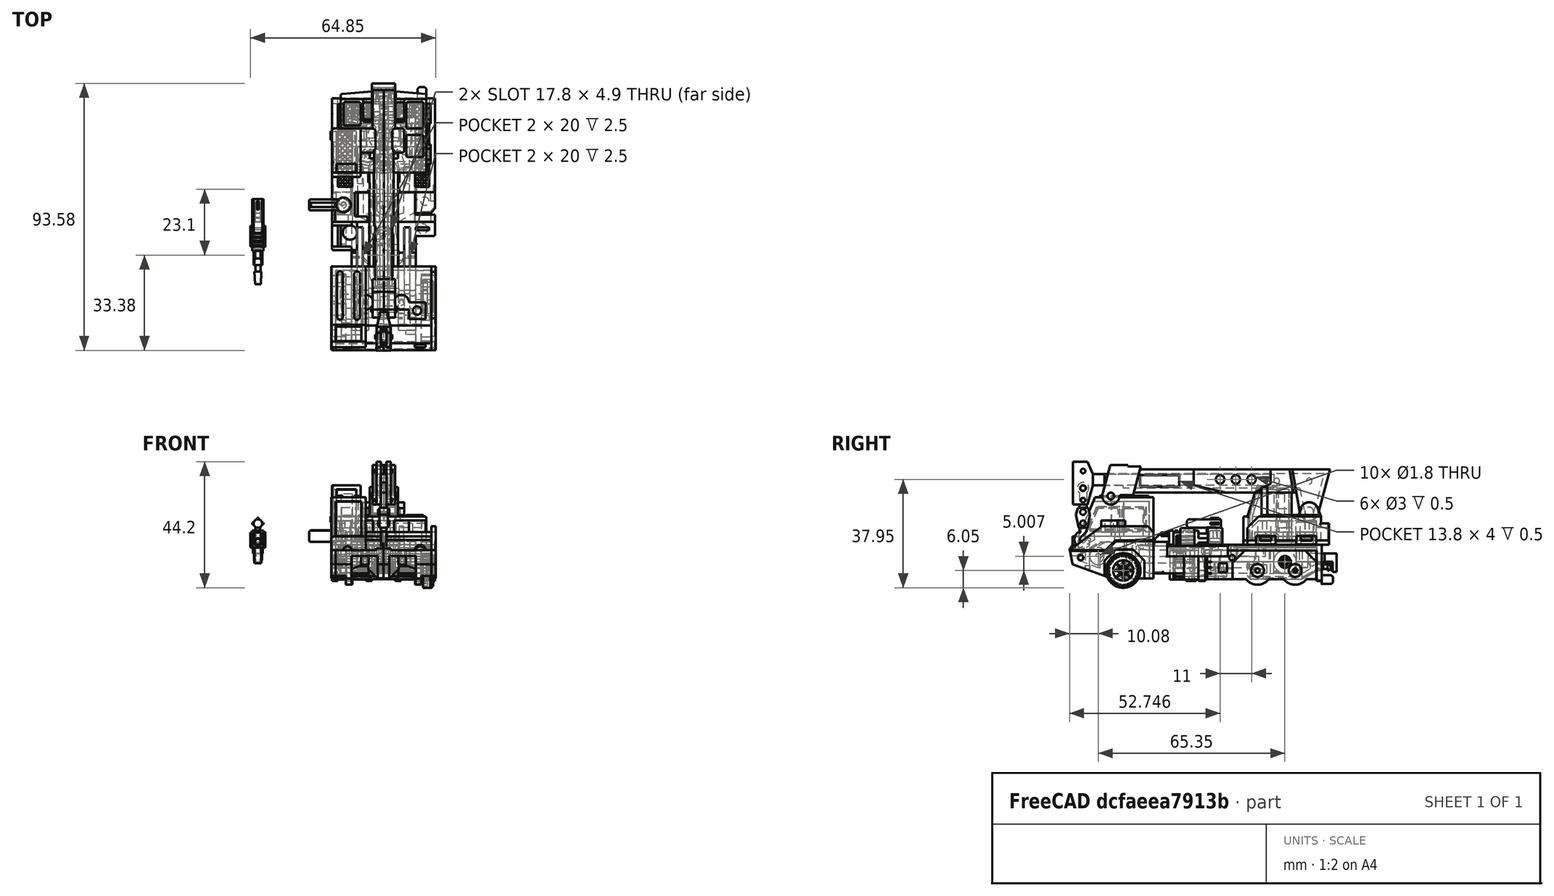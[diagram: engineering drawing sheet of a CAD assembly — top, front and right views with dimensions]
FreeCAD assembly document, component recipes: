
FREECAD ASSEMBLY — COMPONENT RECIPES ("Hook")

This assembly document has 27 components, labeled P0..P26 below (a component is one placed body or linked part). 27 of them carry a construction recipe — the FreeCAD feature program that regenerates the part from scratch, quoted from this document or its linked companion documents; the rest are supplied as boundary geometry only. No exploded tour is included for this assembly.
NOTE — document 4 of 5 of this assembly tour. The two overview renders and the header above are repeated from document 1; the component sections below continue where the previous document stopped.
COMPONENT P17 — recipe-attached ("Left_Outer_Leg", modeled in this document).
Construction recipe (the document's own serialized feature program — sketch geometry with constraints, then the solid features built on it; lengths are millimeters unless a unit is written):

FEATURE [PartDesign::SubShapeBinder] Binder013
  BindCopyOnChange = 0
  BindMode = 0
  ClaimChildren = false
  Context = -> Body019 [Binder013.]
  Fuse = false
  MakeFace = true
  OffsetFill = false
  OffsetIntersection = false
  OffsetJoinType = 0
  OffsetOpenResult = false
  PartialLoad = false
  Refine = true
  Relative = true
  Support = -> [Part__Mirroring001[Face7]]
  _Version = 2
FEATURE [Sketcher::SketchObject] Sketch288
  ArcFitTolerance = 1e-06
  AttachmentSupport = -> [Binder013]
  ExternalGeometry = -> [Binder013]
  FullyConstrained = true
  MakeInternals = false
  MapMode = 5
  Placement = pos=(1.25,0,0) rot=(0.57735,-0.57735,-0.57735;2.0944rad)
  sketch-geometry (39):
    g0: LineSegment StartX=17.1313 StartY=-9.8 StartZ=0 EndX=17.1313 EndY=18.7 EndZ=0
    g1: LineSegment StartX=17.1313 StartY=-9.8 StartZ=0 EndX=18.8313 EndY=-9.8 EndZ=0
    g2: LineSegment StartX=18.8313 StartY=-9.8 StartZ=0 EndX=18.8313 EndY=-3.6 EndZ=0
    g3: Circle CenterX=41.1657 CenterY=-2.53692 CenterZ=0 NormalX=0 NormalY=0 NormalZ=1 AngleXU=0 Radius=0.95
    g4: LineSegment StartX=18.8313 StartY=-3.6 StartZ=0 EndX=22.7813 EndY=0.35 EndZ=0
    g5: LineSegment StartX=22.7813 StartY=0.35 StartZ=0 EndX=28.8813 EndY=0.35 EndZ=0
    g6: LineSegment StartX=28.8813 StartY=0.35 StartZ=0 EndX=32.8313 EndY=-3.6 EndZ=0
    g7: LineSegment StartX=32.8313 StartY=-3.6 StartZ=0 EndX=32.8313 EndY=-8.93216 EndZ=0
    g8: LineSegment StartX=32.8313 StartY=-8.93216 StartZ=0 EndX=44.062 EndY=-4.89651 EndZ=0
    g9: LineSegment StartX=44.062 StartY=-4.89651 StartZ=0 EndX=44.9561 EndY=0.0557565 EndZ=0
    g10: LineSegment StartX=44.9561 StartY=0.0557565 StartZ=0 EndX=43.9561 EndY=0.0557565 EndZ=0
    g11: LineSegment StartX=43.9561 StartY=0.0557565 StartZ=0 EndX=43.9561 EndY=5 EndZ=0
    g12: LineSegment StartX=43.9561 StartY=5 StartZ=0 EndX=41.9561 EndY=5 EndZ=0
    g13: LineSegment StartX=17.1313 StartY=18.7 StartZ=0 EndX=36.1313 EndY=18.7 EndZ=0
    g14: LineSegment StartX=36.1313 StartY=18.7 StartZ=0 EndX=41.9561 EndY=5 EndZ=0
    g15: LineSegment StartX=18.9313 StartY=14.2 StartZ=0 EndX=18.9313 EndY=8.1 EndZ=0
    g16: LineSegment StartX=19.4313 StartY=7.6 StartZ=0 EndX=25.5313 EndY=7.6 EndZ=0
    g17: LineSegment StartX=26.0313 StartY=8.1 StartZ=0 EndX=26.0313 EndY=14.2 EndZ=0
    g18: LineSegment StartX=25.5313 StartY=14.7 StartZ=0 EndX=19.4313 EndY=14.7 EndZ=0
    g19: LineSegment StartX=28.5313 StartY=14.7 StartZ=0 EndX=34.8006 EndY=14.7 EndZ=0
    g20: LineSegment StartX=35.2607 StartY=14.3956 StartZ=0 EndX=37.8542 EndY=8.29564 EndZ=0
    g21: LineSegment StartX=37.3941 StartY=7.6 StartZ=0 EndX=28.5313 EndY=7.6 EndZ=0
    g22: LineSegment StartX=28.0313 StartY=8.1 StartZ=0 EndX=28.0313 EndY=14.2 EndZ=0
    g23: ArcOfCircle CenterX=37.3941 CenterY=8.1 CenterZ=0 NormalX=0 NormalY=0 NormalZ=1 AngleXU=0 Radius=0.5 StartAngle=4.71239 EndAngle=6.6852
    g24: GeomPoint [constr] X=38.15 Y=7.6 Z=0
    g25: ArcOfCircle CenterX=34.8006 CenterY=14.2 CenterZ=0 NormalX=0 NormalY=0 NormalZ=1 AngleXU=0 Radius=0.5 StartAngle=0.402012 EndAngle=1.5708
    g26: GeomPoint [constr] X=35.1313 Y=14.7 Z=0
    g27: ArcOfCircle CenterX=28.5313 CenterY=14.2 CenterZ=0 NormalX=0 NormalY=0 NormalZ=1 AngleXU=0 Radius=0.5 StartAngle=1.5708 EndAngle=3.14159
    g28: GeomPoint [constr] X=28.0313 Y=14.7 Z=0
    g29: ArcOfCircle CenterX=28.5313 CenterY=8.1 CenterZ=0 NormalX=0 NormalY=0 NormalZ=1 AngleXU=0 Radius=0.5 StartAngle=3.14159 EndAngle=4.71239
    g30: GeomPoint [constr] X=28.0313 Y=7.6 Z=0
    g31: ArcOfCircle CenterX=25.5313 CenterY=8.1 CenterZ=0 NormalX=0 NormalY=0 NormalZ=1 AngleXU=0 Radius=0.5 StartAngle=4.71239 EndAngle=6.28319
    g32: GeomPoint [constr] X=26.0313 Y=7.6 Z=0
    g33: ArcOfCircle CenterX=25.5313 CenterY=14.2 CenterZ=0 NormalX=0 NormalY=0 NormalZ=1 AngleXU=0 Radius=0.5 StartAngle=1.2e-15 EndAngle=1.5708
    g34: GeomPoint [constr] X=26.0313 Y=14.7 Z=0
    g35: ArcOfCircle CenterX=19.4313 CenterY=14.2 CenterZ=0 NormalX=0 NormalY=0 NormalZ=1 AngleXU=0 Radius=0.5 StartAngle=1.5708 EndAngle=3.14159
    g36: GeomPoint [constr] X=18.9313 Y=14.7 Z=0
    g37: ArcOfCircle CenterX=19.4313 CenterY=8.1 CenterZ=0 NormalX=0 NormalY=0 NormalZ=1 AngleXU=0 Radius=0.5 StartAngle=3.14159 EndAngle=4.71239
    g38: GeomPoint [constr] X=18.9313 Y=7.6 Z=0
  constraints (91):
    c: Coincident(g0,g-4)
    c: Vertical(g0)
    c: DistanceY(g0,g0) = 28.5
    c: Coincident(g1,g0)
    c: Coincident(g1,g-5)
    c: Coincident(g2,g1)
    c: Coincident(g3,g-13)
    c: Coincident(g2,g-6)
    c: Coincident(g4,g2)
    c: Coincident(g4,g-7)
    c: Coincident(g5,g4)
    c: Coincident(g5,g-8)
    c: Coincident(g6,g5)
    c: Coincident(g6,g-9)
    c: Coincident(g7,g6)
    c: Coincident(g7,g-10)
    c: Coincident(g8,g7)
    c: Coincident(g8,g-11)
    c: Coincident(g9,g8)
    c: Coincident(g9,g-12)
    c: Coincident(g10,g9)
    c: DistanceX(g10,g10) = 1
    c: Coincident(g11,g10)
    c: Vertical(g11)
    c: Coincident(g12,g11)
    c: Horizontal(g12)
    c: Coincident(g13,g0)
    c: Horizontal(g13)
    c: Coincident(g14,g13)
    c: Coincident(g14,g12)
    c: Radius(g3) = 0.95
    c: DistanceY(g-14,g12) = 0
    c: DistanceX(g12,g12) = 2
    c: DistanceX(g13,g13) = 19
    c: PointOnObject(g10,g-12)
    c: Vertical(g15)
    c: Vertical(g17)
    c: Horizontal(g16)
    c: Horizontal(g18)
    c: Horizontal(g19)
    c: Horizontal(g21)
    c: Vertical(g22)
    c: DistanceX(g36,g34) = 7.1
    c: DistanceY(g38,g36) = 7.1
    c: DistanceX(g28,g26) = 7.1
    c: Parallel(g20,g14)
    c: DistanceX(g0,g36) = 1.8
    c: DistanceY(g36,g0) = 4
    c: DistanceY(g30,g28) = 7.1
    c: DistanceY(g26,g13) = 4
    c: DistanceX(g34,g28) = 2
    c: PointOnObject(g24,g20)
    c: PointOnObject(g24,g21)
    c: Tangent(g20,g23) = 1.5708
    c: Tangent(g21,g23) = 1.5708
    c: PointOnObject(g26,g19)
    c: PointOnObject(g26,g20)
    c: Tangent(g19,g25) = 1.5708
    c: Tangent(g20,g25) = 1.5708
    c: PointOnObject(g28,g19)
    c: PointOnObject(g28,g22)
    c: Tangent(g19,g27) = 1.5708
    c: Tangent(g22,g27) = 1.5708
    c: PointOnObject(g30,g21)
    c: PointOnObject(g30,g22)
    c: Tangent(g21,g29) = 1.5708
    c: Tangent(g22,g29) = 1.5708
    c: PointOnObject(g32,g16)
    c: PointOnObject(g32,g17)
    c: Tangent(g16,g31) = -1.5708
    c: Tangent(g17,g31) = -1.5708
    c: PointOnObject(g34,g17)
    c: PointOnObject(g34,g18)
    c: Tangent(g17,g33) = -1.5708
    c: Tangent(g18,g33) = -1.5708
    c: PointOnObject(g36,g15)
    c: PointOnObject(g36,g18)
    c: Tangent(g15,g35) = -1.5708
    c: Tangent(g18,g35) = -1.5708
    c: PointOnObject(g38,g15)
    c: PointOnObject(g38,g16)
    c: Tangent(g15,g37) = -1.5708
    c: Tangent(g16,g37) = -1.5708
    c: Radius(g37) = 0.5
    c: Radius(g35) = 0.5
    c: Radius(g33) = 0.5
    c: Radius(g31) = 0.5
    c: Radius(g29) = 0.5
    c: Radius(g27) = 0.5
    c: Radius(g23) = 0.5
    c: Radius(g25) = 0.5
FEATURE [PartDesign::Pad] Pad188
  Direction = (-1,0,0)
  Length = 1.5
  Length2 = 10
  Profile = -> Sketch288
  ReferenceAxis = -> Sketch288 [N_Axis]
  Refine = true
  Suppressed = false
  Type = 0
FEATURE [Sketcher::SketchObject] Sketch289
  ArcFitTolerance = 1e-06
  AttachmentSupport = -> [Pad188]
  ExternalGeometry = -> [Pad188]
  FullyConstrained = true
  MakeInternals = false
  MapMode = 5
  Placement = pos=(0,-17.1313,0) rot=(0,0.707107,0.707107;3.14159rad)
  sketch-geometry (8):
    g0: LineSegment StartX=0.25 StartY=18.7 StartZ=0 EndX=-11.75 EndY=18.7 EndZ=0
    g1: LineSegment StartX=-11.75 StartY=18.7 StartZ=0 EndX=-11.75 EndY=5 EndZ=0
    g2: LineSegment StartX=-11.75 StartY=5 StartZ=0 EndX=-18 EndY=5 EndZ=0
    g3: LineSegment StartX=-18 StartY=5 StartZ=0 EndX=-18 EndY=3 EndZ=0
    g4: LineSegment StartX=-18 StartY=3 StartZ=0 EndX=-6.75 EndY=3 EndZ=0
    g5: LineSegment StartX=-6.75 StartY=3 StartZ=0 EndX=-6.75 EndY=-9.8 EndZ=0
    g6: LineSegment StartX=-6.75 StartY=-9.8 StartZ=0 EndX=0.25 EndY=-9.8 EndZ=0
    g7: LineSegment StartX=0.25 StartY=-9.8 StartZ=0 EndX=0.25 EndY=18.7 EndZ=0
  constraints (22):
    c: Coincident(g0,g-4)
    c: Horizontal(g0)
    c: Coincident(g1,g0)
    c: Vertical(g1)
    c: Coincident(g2,g1)
    c: Horizontal(g2)
    c: Coincident(g3,g2)
    c: Vertical(g3)
    c: Coincident(g4,g3)
    c: Horizontal(g4)
    c: Coincident(g5,g4)
    c: Vertical(g5)
    c: Coincident(g6,g5)
    c: Coincident(g6,g-4)
    c: Horizontal(g6)
    c: DistanceX(g0,g0) = 12
    c: DistanceY(g1,g1) = 13.7
    c: DistanceX(g2,g2) = 6.25
    c: DistanceY(g3,g3) = 2
    c: DistanceX(g4,g4) = 11.25
    c: Coincident(g7,g6)
    c: Coincident(g7,g0)
FEATURE [PartDesign::Pad] Pad189
  BaseFeature = -> Pad188
  Direction = (0,1,-2e-16)
  Length = 1.5
  Length2 = 10
  Profile = -> Sketch289
  ReferenceAxis = -> Sketch289 [N_Axis]
  Refine = true
  Suppressed = false
  Type = 0
FEATURE [Sketcher::SketchObject] Sketch290
  ArcFitTolerance = 1e-06
  AttachmentSupport = -> [Pad189]
  ExternalGeometry = -> [Pad189]
  FullyConstrained = true
  MakeInternals = false
  MapMode = 5
  Placement = pos=(1.25,0,0) rot=(0.57735,0.57735,0.57735;2.0944rad)
  sketch-geometry (5):
    g0: LineSegment StartX=-41.9561 StartY=5 StartZ=0 EndX=-43.9561 EndY=5 EndZ=0
    g1: LineSegment StartX=-43.9561 StartY=5 StartZ=0 EndX=-43.9561 EndY=0.0557565 EndZ=0
    g2: LineSegment StartX=-42.7061 StartY=0.0557565 StartZ=0 EndX=-43.9561 EndY=0.0557565 EndZ=0
    g3: LineSegment StartX=-41.9561 StartY=5 StartZ=0 EndX=-41.9561 EndY=0.488769 EndZ=0
    g4: LineSegment StartX=-42.7061 StartY=0.0557565 StartZ=0 EndX=-41.9561 EndY=0.488769 EndZ=0
  constraints (12):
    c: Coincident(g0,g-3)
    c: Coincident(g0,g-4)
    c: Coincident(g1,g0)
    c: Coincident(g1,g-4)
    c: Horizontal(g2)
    c: Coincident(g2,g1)
    c: Coincident(g3,g0)
    c: Vertical(g3)
    c: Coincident(g4,g2)
    c: Coincident(g4,g3)
    c: DistanceX(g2,g2) = 1.25
    c: Angle(g4,g2) = 2.61799
FEATURE [PartDesign::Pad] Pad190
  BaseFeature = -> Pad189
  Direction = (1,0,0)
  Length = 10.5
  Length2 = 10
  Profile = -> Sketch290
  ReferenceAxis = -> Sketch290 [N_Axis]
  Refine = true
  Suppressed = false
  Type = 0
FEATURE [Sketcher::SketchObject] Sketch291
  ArcFitTolerance = 1e-06
  AttachmentSupport = -> [Pad190]
  ExternalGeometry = -> [Pad190]
  FullyConstrained = true
  MakeInternals = false
  MapMode = 5
  Placement = pos=(0,1.1e-15,5) rot=(0,0,1;0rad)
  sketch-geometry (6):
    g0: LineSegment StartX=11.75 StartY=-15.6313 StartZ=0 EndX=18 EndY=-15.6313 EndZ=0
    g1: LineSegment StartX=18 StartY=-15.6313 StartZ=0 EndX=18 EndY=-36.4313 EndZ=0
    g2: LineSegment StartX=11.75 StartY=-15.6313 StartZ=0 EndX=11.75 EndY=-17.1313 EndZ=0
    g3: LineSegment StartX=11.75 StartY=-17.1313 StartZ=0 EndX=10.25 EndY=-17.1313 EndZ=0
    g4: LineSegment StartX=10.25 StartY=-17.1313 StartZ=0 EndX=10.25 EndY=-36.4313 EndZ=0
    g5: LineSegment StartX=10.25 StartY=-36.4313 StartZ=0 EndX=18 EndY=-36.4313 EndZ=0
  constraints (16):
    c: Coincident(g0,g-4)
    c: Coincident(g0,g-4)
    c: Coincident(g1,g0)
    c: Vertical(g1)
    c: Coincident(g2,g0)
    c: Vertical(g2)
    c: Coincident(g3,g2)
    c: Horizontal(g3)
    c: Coincident(g4,g3)
    c: Vertical(g4)
    c: Coincident(g5,g4)
    c: Coincident(g5,g1)
    c: Horizontal(g5)
    c: DistanceX(g3,g3) = 1.5
    c: DistanceY(g2,g2) = 1.5
    c: DistanceY(g4,g4) = 19.3
FEATURE [PartDesign::Pad] Pad191
  BaseFeature = -> Pad190
  Direction = (0,0,1)
  Length = 1.5
  Length2 = 10
  Profile = -> Sketch291
  ReferenceAxis = -> Sketch291 [N_Axis]
  Refine = true
  Suppressed = false
  Type = 0
FEATURE [Sketcher::SketchObject] Sketch292
  ArcFitTolerance = 1e-06
  AttachmentSupport = -> [Pad191]
  ExternalGeometry = -> [Pad191]
  FullyConstrained = true
  MakeInternals = false
  MapMode = 5
  Placement = pos=(0,0,6.5) rot=(0,0,1;0rad)
  sketch-geometry (1):
    g0: Circle CenterX=11.75 CenterY=-28.2313 CenterZ=0 NormalX=0 NormalY=0 NormalZ=1 AngleXU=0 Radius=0.75
  constraints (3):
    c: Radius(g0) = 0.75
    c: DistanceX(g-3,g0) = 1.5
    c: DistanceY(g-3,g0) = 8.2
FEATURE [PartDesign::Pocket] Pocket130
  BaseFeature = -> Pad191
  Direction = (0,0,-1)
  Length = 5
  Length2 = 5
  Profile = -> Sketch292
  ReferenceAxis = -> Sketch292 [N_Axis]
  Refine = true
  Suppressed = false
  Type = 0
FEATURE [Sketcher::SketchObject] Sketch293
  ArcFitTolerance = 1e-06
  AttachmentSupport = -> [Pocket130]
  ExternalGeometry = -> [Pocket130]
  FullyConstrained = true
  MakeInternals = false
  MapMode = 5
  Placement = pos=(1.25,0,0) rot=(0.57735,0.57735,0.57735;2.0944rad)
  sketch-geometry (4):
    g0: LineSegment StartX=-36.1313 StartY=18.7 StartZ=0 EndX=-36.7691 EndY=17.2 EndZ=0
    g1: LineSegment StartX=-36.7691 StartY=17.2 StartZ=0 EndX=-17.1313 EndY=17.2 EndZ=0
    g2: LineSegment StartX=-17.1313 StartY=17.2 StartZ=0 EndX=-17.1313 EndY=18.7 EndZ=0
    g3: LineSegment StartX=-17.1313 StartY=18.7 StartZ=0 EndX=-36.1313 EndY=18.7 EndZ=0
  constraints (10):
    c: Coincident(g0,g-5)
    c: PointOnObject(g0,g-5)
    c: Coincident(g1,g0)
    c: PointOnObject(g1,g-3)
    c: Horizontal(g1)
    c: Coincident(g2,g1)
    c: Coincident(g2,g-4)
    c: Coincident(g3,g2)
    c: Coincident(g3,g0)
    c: DistanceY(g2,g2) = 1.5
FEATURE [PartDesign::Pad] Pad192
  BaseFeature = -> Pocket130
  Direction = (1,0,0)
  Length = 10.5
  Length2 = 10
  Profile = -> Sketch293
  ReferenceAxis = -> Sketch293 [N_Axis]
  Refine = true
  Suppressed = false
  Type = 0
FEATURE [Sketcher::SketchObject] Sketch294
  ArcFitTolerance = 1e-06
  AttachmentSupport = -> [Pad192]
  ExternalGeometry = -> [Pad192]
  FullyConstrained = false
  MakeInternals = false
  MapMode = 5
  Placement = pos=(11.75,0,0) rot=(0.57735,0.57735,0.57735;2.0944rad)
  sketch-geometry (7):
    g0: LineSegment StartX=-36.4313 StartY=3.64 StartZ=0 EndX=-41.9561 EndY=0.488769 EndZ=0
    g1: LineSegment StartX=-41.9561 StartY=0.488769 StartZ=0 EndX=-41.9561 EndY=5 EndZ=0
    g2: LineSegment StartX=-41.9561 StartY=5 StartZ=0 EndX=-36.7691 EndY=17.2 EndZ=0
    g3: LineSegment StartX=-36.7691 StartY=17.2 StartZ=0 EndX=-17.1313 EndY=17.2 EndZ=0
    g4: LineSegment StartX=-17.1313 StartY=17.2 StartZ=0 EndX=-17.1313 EndY=6.5 EndZ=0
    g5: LineSegment StartX=-17.1313 StartY=6.5 StartZ=0 EndX=-36.4313 EndY=6.5 EndZ=0
    g6: LineSegment StartX=-36.4313 StartY=6.5 StartZ=0 EndX=-36.4313 EndY=3.64 EndZ=0
  constraints (11):
    c: Coincident(g1,g0)
    c: Coincident(g1,g-3)
    c: Coincident(g2,g1)
    c: Coincident(g2,g-7)
    c: Coincident(g3,g2)
    c: Coincident(g3,g-7)
    c: Coincident(g4,g3)
    c: Coincident(g4,g-6)
    c: Coincident(g5,g4)
    c: Coincident(g0,g-3)
    c: DistanceY(g0,g-5) = 2.86
FEATURE [PartDesign::Pad] Pad193
  BaseFeature = -> Pad192
  Direction = (1,0,0)
  Length = 1.5
  Length2 = 10
  Profile = -> Sketch294
  ReferenceAxis = -> Sketch294 [N_Axis]
  Refine = true
  Reversed = true
  Suppressed = false
  Type = 0
FEATURE [Sketcher::SketchObject] Sketch295
  ArcFitTolerance = 1e-06
  AttachmentSupport = -> [Pad193]
  ExternalGeometry = -> [Pad193]
  FullyConstrained = true
  MakeInternals = false
  MapMode = 5
  Placement = pos=(0,0,6.5) rot=(0,0,1;0rad)
  sketch-geometry (1):
    g0: Circle CenterX=11.75 CenterY=-28.2313 CenterZ=0 NormalX=0 NormalY=0 NormalZ=1 AngleXU=0 Radius=2.6
  constraints (2):
    c: Coincident(g0,g-3)
    c: Radius(g0) = 2.6
FEATURE [PartDesign::Pad] Pad194
  BaseFeature = -> Pad193
  Direction = (0,0,1)
  Length = 4
  Length2 = 10
  Profile = -> Sketch295
  ReferenceAxis = -> Sketch295 [N_Axis]
  Refine = true
  Suppressed = false
  Type = 0
FEATURE [PartDesign::Pad] Pad195
  BaseFeature = -> Pad194
  Direction = (0,0,-1)
  Length = 1.5
  Length2 = 10
  Profile = -> Pad194 [Face52]
  Refine = true
  Suppressed = false
  Type = 0
FEATURE [PartDesign::Pad] Pad196
  BaseFeature = -> Pad195
  Direction = (0,0,1)
  Length = 7
  Length2 = 10
  Profile = -> Pad195 [Face50]
  Refine = true
  Suppressed = false
  Type = 0
FEATURE [PartDesign::Pocket] Pocket131
  BaseFeature = -> Pad196
  Direction = (0,0,1)
  Length = 2
  Length2 = 5
  Profile = -> Pad196 [Face53]
  Refine = true
  Suppressed = false
  Type = 0
FEATURE [Sketcher::SketchObject] Sketch296
  ArcFitTolerance = 1e-06
  AttachmentSupport = -> [Pocket131]
  ExternalGeometry = -> [Pocket131]
  FullyConstrained = true
  MakeInternals = false
  MapMode = 5
  Placement = pos=(0,0,18.7) rot=(0,0,1;0rad)
  sketch-geometry (8):
    g0: ArcOfCircle CenterX=8.75 CenterY=-18.3813 CenterZ=0 NormalX=0 NormalY=0 NormalZ=1 AngleXU=0 Radius=1 StartAngle=1.7e-15 EndAngle=3.14159
    g1: ArcOfCircle CenterX=8.75 CenterY=-33.3813 CenterZ=0 NormalX=0 NormalY=0 NormalZ=1 AngleXU=0 Radius=1 StartAngle=3.14159 EndAngle=6.28319
    g2: LineSegment StartX=9.75 StartY=-18.3813 StartZ=0 EndX=9.75 EndY=-33.3813 EndZ=0
    g3: LineSegment StartX=7.75 StartY=-18.3813 StartZ=0 EndX=7.75 EndY=-33.3813 EndZ=0
    g4: ArcOfCircle CenterX=2.75 CenterY=-18.3813 CenterZ=0 NormalX=0 NormalY=0 NormalZ=1 AngleXU=0 Radius=1 StartAngle=0 EndAngle=3.14159
    g5: ArcOfCircle CenterX=2.75 CenterY=-33.3813 CenterZ=0 NormalX=0 NormalY=0 NormalZ=1 AngleXU=0 Radius=1 StartAngle=3.14159 EndAngle=6.28319
    g6: LineSegment StartX=3.75 StartY=-18.3813 StartZ=0 EndX=3.75 EndY=-33.3813 EndZ=0
    g7: LineSegment StartX=1.75 StartY=-18.3813 StartZ=0 EndX=1.75 EndY=-33.3813 EndZ=0
  constraints (21):
    c: Tangent(g0,g2) = 1.5708
    c: Tangent(g0,g3) = -1.5708
    c: Tangent(g1,g2) = 1.5708
    c: Tangent(g1,g3) = -1.5708
    c: Equal(g0,g1)
    c: Vertical(g2)
    c: Tangent(g4,g6) = 1.5708
    c: Tangent(g4,g7) = -1.5708
    c: Tangent(g5,g6) = 1.5708
    c: Tangent(g5,g7) = -1.5708
    c: Equal(g4,g5)
    c: Vertical(g6)
    c: Diameter(g4) = 2
    c: Diameter(g0) = 2
    c: DistanceY(g1,g0) = 15
    c: DistanceY(g5,g4) = 15
    c: DistanceY(g-3,g-3) = 20.5
    c: DistanceY(g0,g-4) = 2.75
    c: DistanceY(g4,g-6) = 2.75
    c: DistanceX(g-6,g4) = 2
    c: DistanceX(g0,g-4) = 2
FEATURE [PartDesign::Pad] Pad197
  BaseFeature = -> Pocket131
  Direction = (0,0,1)
  Length = 0.5
  Length2 = 10
  Profile = -> Sketch296
  ReferenceAxis = -> Sketch296 [N_Axis]
  Refine = true
  Suppressed = false
  Type = 0
FEATURE [Sketcher::SketchObject] Sketch297
  ArcFitTolerance = 1e-06
  AttachmentSupport = -> [Pad197]
  ExternalGeometry = -> [Pad197]
  FullyConstrained = true
  MakeInternals = false
  MapMode = 5
  Placement = pos=(-0.25,0,0) rot=(0.57735,-0.57735,-0.57735;2.0944rad)
  sketch-geometry (32):
    g0: LineSegment StartX=43.9561 StartY=0.0557565 StartZ=0 EndX=32.4084 EndY=0.0557565 EndZ=0
    g1: LineSegment StartX=32.4084 StartY=0.0557565 StartZ=0 EndX=28.9641 EndY=3.5 EndZ=0
    g2: LineSegment StartX=28.9641 StartY=3.5 StartZ=0 EndX=15.6313 EndY=3.5 EndZ=0
    g3: LineSegment StartX=15.6313 StartY=3.5 StartZ=0 EndX=15.6313 EndY=3.3 EndZ=0
    g4: LineSegment StartX=15.6313 StartY=3.3 StartZ=0 EndX=28.8813 EndY=3.3 EndZ=0
    g5: LineSegment StartX=28.8813 StartY=3.3 StartZ=0 EndX=32.3255 EndY=-0.144243 EndZ=0
    g6: LineSegment StartX=32.3255 StartY=-0.144243 StartZ=0 EndX=44.92 EndY=-0.144243 EndZ=0
    g7: LineSegment StartX=44.92 StartY=-0.144243 StartZ=0 EndX=44.9561 EndY=0.0557565 EndZ=0
    g8: LineSegment [constr] StartX=31.7599 StartY=0.704285 StartZ=0 EndX=31.6184 EndY=0.562863 EndZ=0
    g9: LineSegment StartX=43.9561 StartY=0.0557565 StartZ=0 EndX=44.9561 EndY=0.0557565 EndZ=0
    g10: LineSegment StartX=18.4313 StartY=15.2 StartZ=0 EndX=18.4313 EndY=7.1 EndZ=0
    g11: LineSegment StartX=18.4313 StartY=7.1 StartZ=0 EndX=26.5313 EndY=7.1 EndZ=0
    g12: LineSegment StartX=26.5313 StartY=7.1 StartZ=0 EndX=26.5313 EndY=15.2 EndZ=0
    g13: LineSegment StartX=26.5313 StartY=15.2 StartZ=0 EndX=18.4313 EndY=15.2 EndZ=0
    g14: LineSegment StartX=18.2313 StartY=15.4 StartZ=0 EndX=18.2313 EndY=6.9 EndZ=0
    g15: LineSegment StartX=18.2313 StartY=6.9 StartZ=0 EndX=26.7313 EndY=6.9 EndZ=0
    g16: LineSegment StartX=26.7313 StartY=6.9 StartZ=0 EndX=26.7313 EndY=15.4 EndZ=0
    g17: LineSegment StartX=26.7313 StartY=15.4 StartZ=0 EndX=18.2313 EndY=15.4 EndZ=0
    g18: LineSegment StartX=27.5313 StartY=15.2 StartZ=0 EndX=35.462 EndY=15.2 EndZ=0
    g19: LineSegment StartX=35.462 StartY=15.2 StartZ=0 EndX=38.3144 EndY=8.49127 EndZ=0
    g20: LineSegment StartX=37.3941 StartY=7.1 StartZ=0 EndX=27.5313 EndY=7.1 EndZ=0
    g21: LineSegment StartX=27.5313 StartY=7.1 StartZ=0 EndX=27.5313 EndY=15.2 EndZ=0
    g22: LineSegment StartX=27.3313 StartY=15.4 StartZ=0 EndX=35.5943 EndY=15.4 EndZ=0
    g23: LineSegment StartX=35.5943 StartY=15.4 StartZ=0 EndX=38.4984 EndY=8.56952 EndZ=0
    g24: LineSegment StartX=37.3941 StartY=6.9 StartZ=0 EndX=27.3313 EndY=6.9 EndZ=0
    g25: LineSegment StartX=27.3313 StartY=6.9 StartZ=0 EndX=27.3313 EndY=15.4 EndZ=0
    g26: ArcOfCircle CenterX=37.3941 CenterY=8.1 CenterZ=0 NormalX=0 NormalY=0 NormalZ=1 AngleXU=0 Radius=1 StartAngle=4.71239 EndAngle=6.6852
    g27: GeomPoint [constr] X=38.9059 Y=7.1 Z=0
    g28: ArcOfCircle CenterX=37.3941 CenterY=8.1 CenterZ=0 NormalX=0 NormalY=0 NormalZ=1 AngleXU=0 Radius=1.2 StartAngle=4.71239 EndAngle=6.6852
    g29: GeomPoint [constr] X=39.2082 Y=6.9 Z=0
    g30: LineSegment [constr] StartX=36.0374 StartY=14.358 StartZ=0 EndX=35.8533 EndY=14.2797 EndZ=0
    g31: LineSegment [constr] StartX=36.2446 StartY=13.3594 StartZ=0 EndX=35.7844 EndY=13.1638 EndZ=0
  constraints (91):
    c: Coincident(g0,g-3)
    c: Horizontal(g0)
    c: Coincident(g1,g0)
    c: Coincident(g2,g1)
    c: PointOnObject(g2,g-5)
    c: Horizontal(g2)
    c: Coincident(g3,g2)
    c: PointOnObject(g3,g-5)
    c: Coincident(g4,g3)
    c: Horizontal(g4)
    c: Coincident(g5,g4)
    c: Coincident(g6,g5)
    c: PointOnObject(g6,g-4)
    c: Horizontal(g6)
    c: Coincident(g7,g6)
    c: Coincident(g7,g-4)
    c: DistanceY(g6,g7) = 0.2
    c: DistanceY(g3,g2) = 0.2
    c: PointOnObject(g8,g1)
    c: PointOnObject(g8,g5)
    c: Parallel(g1,g5)
    c: Angle(g8,g1) = 1.5708
    c: Distance(g8) = 0.2
    c: DistanceX(g-6,g4) = 0
    c: Angle(g0,g1) = 2.35619
    c: DistanceY(g2,g-7) = 3
    c: Distance(g8,g5) = 1
    c: Coincident(g9,g0)
    c: Coincident(g9,g7)
    c: Coincident(g10,g11)
    c: Coincident(g11,g12)
    c: Coincident(g12,g13)
    c: Coincident(g13,g10)
    c: Vertical(g10)
    c: Vertical(g12)
    c: Horizontal(g11)
    c: Horizontal(g13)
    c: Coincident(g14,g15)
    c: Coincident(g15,g16)
    c: Coincident(g16,g17)
    c: Coincident(g17,g14)
    c: Vertical(g14)
    c: Vertical(g16)
    c: Horizontal(g15)
    c: Horizontal(g17)
    c: Horizontal(g18)
    c: Coincident(g19,g18)
    c: Horizontal(g20)
    c: Coincident(g21,g20)
    c: Coincident(g21,g18)
    c: Vertical(g21)
    c: Horizontal(g22)
    c: Coincident(g23,g22)
    c: Horizontal(g24)
    c: Coincident(g25,g24)
    c: Coincident(g25,g22)
    c: Vertical(g25)
    c: DistanceY(g12,g16) = 0.2
    c: DistanceY(g18,g22) = 0.2
    c: DistanceY(g15,g11) = 0.2
    c: DistanceX(g14,g10) = 0.2
    c: DistanceX(g11,g15) = 0.2
    c: DistanceX(g-9,g11) = 0.5
    c: DistanceX(g10,g-10) = 0.5
    c: DistanceY(g10,g-8) = 0.5
    c: DistanceY(g-11,g10) = 0.5
    c: PointOnObject(g27,g19)
    c: PointOnObject(g27,g20)
    c: Tangent(g19,g26) = 1.5708
    c: Tangent(g20,g26) = 1.5708
    c: PointOnObject(g29,g23)
    c: PointOnObject(g29,g24)
    c: Tangent(g23,g28) = 1.5708
    c: Tangent(g24,g28) = 1.5708
    c: Coincident(g28,g26)
    c: DistanceY(g24,g20) = 0.2
    c: DistanceY(g20,g-12) = 0.5
    c: DistanceY(g-13,g18) = 0.5
    c: DistanceX(g18,g-15) = 0.5
    c: DistanceX(g22,g18) = 0.2
    c: PointOnObject(g30,g23)
    c: PointOnObject(g30,g19)
    c: Angle(g30,g23) = 1.5708
    c: Distance(g30) = 0.2
    c: Distance(g18,g30) = 1
    c: Parallel(g19,g-14)
    c: PointOnObject(g31,g19)
    c: PointOnObject(g31,g-14)
    c: Angle(g31,g19) = 1.5708
    c: Coincident(g26,g-16)
    c: Distance(g31,g18) = 2
FEATURE [PartDesign::Pocket] Pocket132
  BaseFeature = -> Pad197
  Direction = (1,0,0)
  Length = 0.3
  Length2 = 5
  Profile = -> Sketch297
  ReferenceAxis = -> Sketch297 [N_Axis]
  Refine = true
  Suppressed = false
  Type = 0
FEATURE [Sketcher::SketchObject] Sketch303
  ArcFitTolerance = 1e-06
  AttachmentSupport = -> [Pocket132]
  ExternalGeometry = -> [Pocket132]
  FullyConstrained = true
  MakeInternals = false
  MapMode = 5
  Placement = pos=(0,-43.9561,0) rot=(1,0,0;1.5708rad)
  sketch-geometry (2):
    g0: ArcOfCircle CenterX=5.4 CenterY=0.0557565 CenterZ=0 NormalX=0 NormalY=0 NormalZ=1 AngleXU=0 Radius=1.45 StartAngle=0 EndAngle=3.14159
    g1: LineSegment StartX=3.95 StartY=0.0557565 StartZ=0 EndX=6.85 EndY=0.0557565 EndZ=0
  constraints (7):
    c: PointOnObject(g0,g-7)
    c: PointOnObject(g0,g-7)
    c: Diameter(g0) = 2.9
    c: PointOnObject(g0,g-7)
    c: DistanceX(g-5,g0) = 4.2
    c: Coincident(g1,g0)
    c: Coincident(g1,g0)
FEATURE [PartDesign::Pad] Pad201
  BaseFeature = -> Pocket132
  Direction = (0,-1,2e-16)
  Length = 0.5
  Length2 = 10
  Profile = -> Sketch303
  ReferenceAxis = -> Sketch303 [N_Axis]
  Refine = true
  Suppressed = false
  Type = 0
FEATURE [PartDesign::Body] Body019  label="Left_Outer_Leg"
  AllowCompound = false
  Group = -> [Binder013,Sketch288,Pad188,Sketch289,Pad189,Sketch290,Pad190,Sketch291,Pad191,Sketch292,Pocket130,Sketch293,Pad192,Sketch294,Pad193,Sketch295,Pad194,Pad195,Pad196,Pocket131,Sketch296,Pad197,Sketch297,Pocket132,Sketch303,Pad201]
  Origin = -> Origin020
  Placement = pos=(0,8.9e-15,0) rot=(0,0,1;0rad)
  Tip = -> Pad201
COMPONENT P18 — recipe-attached ("Front_Windows", modeled in this document).
Construction recipe (the document's own serialized feature program — sketch geometry with constraints, then the solid features built on it; lengths are millimeters unless a unit is written):

FEATURE [PartDesign::SubShapeBinder] Binder014
  BindCopyOnChange = 0
  BindMode = 2
  ClaimChildren = false
  Context = -> Body020 [Binder014.]
  Fuse = false
  MakeFace = true
  OffsetFill = false
  OffsetIntersection = false
  OffsetJoinType = 0
  OffsetOpenResult = false
  PartialLoad = false
  Refine = true
  Relative = true
  _Version = 2
FEATURE [Sketcher::SketchObject] Sketch298
  ArcFitTolerance = 1e-06
  AttachmentSupport = -> [Binder014]
  ExternalGeometry = -> [Binder014]
  FullyConstrained = true
  MakeInternals = false
  MapMode = 5
  Placement = pos=(1.25,0,0) rot=(0.57735,0.57735,0.57735;2.0944rad)
  sketch-geometry (5):
    g0: LineSegment StartX=-36.736 StartY=17.15 StartZ=0 EndX=-41.8805 EndY=5.05 EndZ=0
    g1: LineSegment StartX=-41.8805 StartY=5.05 StartZ=0 EndX=-17.1813 EndY=5.05 EndZ=0
    g2: LineSegment StartX=-17.1813 StartY=5.05 StartZ=0 EndX=-17.1813 EndY=17.15 EndZ=0
    g3: LineSegment StartX=-17.1813 StartY=17.15 StartZ=0 EndX=-36.736 EndY=17.15 EndZ=0
    g4: LineSegment [constr] StartX=-41.1735 StartY=6.84055 StartZ=0 EndX=-41.1275 EndY=6.82099 EndZ=0
  constraints (16):
    c: Coincident(g1,g0)
    c: Horizontal(g1)
    c: Coincident(g2,g1)
    c: Vertical(g2)
    c: Coincident(g3,g2)
    c: Horizontal(g3)
    c: Coincident(g3,g0)
    c: Parallel(g0,g-5)
    c: DistanceY(g0,g-5) = 0.05
    c: DistanceX(g2,g-4) = 0.05
    c: DistanceY(g-5,g0) = 0.05
    c: PointOnObject(g4,g-5)
    c: PointOnObject(g4,g0)
    c: Angle(g0,g4) = 1.5708
    c: Distance(g4) = 0.05
    c: Distance(g4,g-5) = 2
FEATURE [PartDesign::Pad] Pad198
  Direction = (1,0,0)
  Length = 8.95
  Length2 = 10
  Profile = -> Sketch298
  ReferenceAxis = -> Sketch298 [N_Axis]
  Refine = true
  Suppressed = false
  Type = 0
FEATURE [PartDesign::Pocket] Pocket133
  BaseFeature = -> Pad198
  Direction = (1,0,0)
  Length = 0.05
  Length2 = 5
  Profile = -> Pad198 [Face5]
  Refine = true
  Suppressed = false
  Type = 0
FEATURE [Sketcher::SketchObject] Sketch299
  ArcFitTolerance = 1e-06
  AttachmentSupport = -> [Pocket133]
  ExternalGeometry = -> [Pocket133]
  FullyConstrained = true
  MakeInternals = false
  MapMode = 5
  Placement = pos=(0,0,5.05) rot=(1,0,0;3.14159rad)
  sketch-geometry (2):
    g0: ArcOfCircle CenterX=11.7492 CenterY=28.2305 CenterZ=0 NormalX=0 NormalY=0 NormalZ=1 AngleXU=0 Radius=2.65 StartAngle=2.19518 EndAngle=4.088
    g1: LineSegment StartX=10.2 StartY=30.3805 StartZ=0 EndX=10.2 EndY=26.0805 EndZ=0
  constraints (7):
    c: PointOnObject(g0,g-3)
    c: Radius(g0) = 2.65
    c: PointOnObject(g0,g-3)
    c: DistanceY(g0,g0) = 4.3
    c: DistanceY(g0,g-3) = 11.5
    c: Coincident(g1,g0)
    c: Coincident(g1,g0)
FEATURE [PartDesign::Pocket] Pocket134
  BaseFeature = -> Pocket133
  Direction = (0,0,1)
  Length = 13
  Length2 = 5
  Profile = -> Sketch299
  ReferenceAxis = -> Sketch299 [N_Axis]
  Refine = true
  Suppressed = false
  Type = 0
FEATURE [Sketcher::SketchObject] Sketch300
  ArcFitTolerance = 1e-06
  AttachmentSupport = -> [Pocket134]
  ExternalGeometry = -> [Pocket134]
  FullyConstrained = true
  MakeInternals = false
  MapMode = 5
  Placement = pos=(1.3,0,0) rot=(0.57735,-0.57735,-0.57735;2.0944rad)
  sketch-geometry (5):
    g0: LineSegment StartX=19.1813 StartY=5.05 StartZ=0 EndX=19.1813 EndY=15.15 EndZ=0
    g1: LineSegment StartX=19.1813 StartY=15.15 StartZ=0 EndX=35.4131 EndY=15.15 EndZ=0
    g2: LineSegment StartX=35.4131 StartY=15.15 StartZ=0 EndX=39.7072 EndY=5.05 EndZ=0
    g3: LineSegment StartX=39.7072 StartY=5.05 StartZ=0 EndX=19.1813 EndY=5.05 EndZ=0
    g4: LineSegment [constr] StartX=37.6449 StartY=15.0123 StartZ=0 EndX=35.8043 EndY=14.2297 EndZ=0
  constraints (16):
    c: PointOnObject(g0,g-6)
    c: Vertical(g0)
    c: Coincident(g1,g0)
    c: Horizontal(g1)
    c: Coincident(g2,g1)
    c: PointOnObject(g2,g-6)
    c: Coincident(g3,g2)
    c: Coincident(g3,g0)
    c: DistanceX(g-5,g0) = 2
    c: DistanceY(g0,g-5) = 2
    c: Parallel(g2,g-3)
    c: PointOnObject(g4,g-3)
    c: PointOnObject(g4,g2)
    c: Angle(g4,g-3) = 1.5708
    c: Distance(g4) = 2
    c: Distance(g4,g1) = 1
FEATURE [PartDesign::Pocket] Pocket135
  BaseFeature = -> Pocket134
  Direction = (1,0,0)
  Length = 6.9
  Length2 = 5
  Profile = -> Sketch300
  ReferenceAxis = -> Sketch300 [N_Axis]
  Refine = true
  Suppressed = false
  Type = 0
FEATURE [Sketcher::SketchObject] Sketch301
  ArcFitTolerance = 1e-06
  AttachmentSupport = -> [Pocket135]
  ExternalGeometry = -> [Pocket135]
  FullyConstrained = true
  MakeInternals = false
  MapMode = 5
  Placement = pos=(1.3,0,0) rot=(0.57735,-0.57735,-0.57735;2.0944rad)
  sketch-geometry (4):
    g0: LineSegment StartX=19.1813 StartY=15.15 StartZ=0 EndX=35.4131 EndY=15.15 EndZ=0
    g1: LineSegment StartX=35.4131 StartY=15.15 StartZ=0 EndX=39.7072 EndY=5.05 EndZ=0
    g2: LineSegment StartX=39.7072 StartY=5.05 StartZ=0 EndX=19.1813 EndY=5.05 EndZ=0
    g3: LineSegment StartX=19.1813 StartY=5.05 StartZ=0 EndX=19.1813 EndY=15.15 EndZ=0
  constraints (8):
    c: Coincident(g0,g-5)
    c: Coincident(g0,g-4)
    c: Coincident(g1,g0)
    c: Coincident(g1,g-4)
    c: Coincident(g2,g1)
    c: Coincident(g2,g-5)
    c: Coincident(g3,g2)
    c: Coincident(g3,g0)
FEATURE [PartDesign::Pad] Pad199
  BaseFeature = -> Pocket135
  Direction = (-1,0,0)
  Length = 2
  Length2 = 10
  Profile = -> Sketch301
  ReferenceAxis = -> Sketch301 [N_Axis]
  Refine = true
  Reversed = true
  Suppressed = false
  Type = 0
FEATURE [Sketcher::SketchObject] Sketch302
  ArcFitTolerance = 1e-06
  AttachmentSupport = -> [Pad199]
  ExternalGeometry = -> [Pad199]
  FullyConstrained = true
  MakeInternals = false
  MapMode = 5
  Placement = pos=(0,0,5.05) rot=(1,0,0;3.14159rad)
  sketch-geometry (4):
    g0: LineSegment StartX=8.2 StartY=39.7072 StartZ=0 EndX=8.2 EndY=41.8305 EndZ=0
    g1: LineSegment StartX=8.2 StartY=41.8305 StartZ=0 EndX=3.3 EndY=41.8305 EndZ=0
    g2: LineSegment StartX=3.3 StartY=41.8305 StartZ=0 EndX=3.3 EndY=39.7072 EndZ=0
    g3: LineSegment StartX=3.3 StartY=39.7072 StartZ=0 EndX=8.2 EndY=39.7072 EndZ=0
  constraints (10):
    c: Coincident(g0,g1)
    c: Coincident(g1,g2)
    c: Coincident(g2,g3)
    c: Coincident(g3,g0)
    c: Vertical(g0)
    c: Vertical(g2)
    c: Horizontal(g1)
    c: Coincident(g0,g-4)
    c: Coincident(g-4,g2)
    c: DistanceY(g1,g-3) = 0.05
FEATURE [PartDesign::Pad] Pad200
  BaseFeature = -> Pad199
  Direction = (0,0,-1)
  Length = 1.5
  Length2 = 10
  Profile = -> Sketch302
  ReferenceAxis = -> Sketch302 [N_Axis]
  Refine = true
  Suppressed = false
  Type = 0
FEATURE [PartDesign::Body] Body020  label="Front_Windows"
  AllowCompound = false
  Group = -> [Binder014,Sketch298,Pad198,Pocket133,Sketch299,Pocket134,Sketch300,Pocket135,Sketch301,Pad199,Sketch302,Pad200]
  Origin = -> Origin021
  Placement = pos=(0,8.9e-15,0) rot=(0,0,1;0rad)
  Tip = -> Pad200
COMPONENT P19 — recipe-attached ("Pre_Right_Arm", modeled in this document).
Construction recipe (the document's own serialized feature program — sketch geometry with constraints, then the solid features built on it; lengths are millimeters unless a unit is written):

FEATURE [PartDesign::SubShapeBinder] Binder015
  BindCopyOnChange = 0
  BindMode = 2
  ClaimChildren = false
  Context = -> Body021 [Binder015.]
  Fuse = false
  MakeFace = true
  OffsetFill = false
  OffsetIntersection = false
  OffsetJoinType = 0
  OffsetOpenResult = false
  PartialLoad = false
  Refine = true
  Relative = true
  _Version = 2
FEATURE [Sketcher::SketchObject] Sketch304
  ArcFitTolerance = 1e-06
  AttachmentSupport = -> [Binder015]
  ExternalGeometry = -> [Binder015]
  FullyConstrained = true
  MakeInternals = false
  MapMode = 5
  Placement = pos=(0,0,0) rot=(1,0,0;3.14159rad)
  sketch-geometry (4):
    g0: LineSegment StartX=7 StartY=-41.35 StartZ=0 EndX=7 EndY=-10.35 EndZ=0
    g1: LineSegment StartX=7 StartY=-10.35 StartZ=0 EndX=5 EndY=-10.35 EndZ=0
    g2: LineSegment StartX=5 StartY=-10.35 StartZ=0 EndX=5 EndY=-41.35 EndZ=0
    g3: LineSegment StartX=7 StartY=-41.35 StartZ=0 EndX=5 EndY=-41.35 EndZ=0
  constraints (12):
    c: PointOnObject(g0,g-3)
    c: PointOnObject(g0,g-5)
    c: Coincident(g1,g0)
    c: Horizontal(g1)
    c: Coincident(g2,g1)
    c: Vertical(g2)
    c: Coincident(g3,g0)
    c: Coincident(g3,g2)
    c: Horizontal(g3)
    c: DistanceY(g-4,g0) = 0.05
    c: DistanceY(g0,g-6) = 0.05
    c: DistanceX(g1,g1) = 2
FEATURE [PartDesign::Pad] Pad202
  Direction = (0,0,-1)
  Length = 10
  Length2 = 10
  Profile = -> Sketch304
  ReferenceAxis = -> Sketch304 [N_Axis]
  Refine = true
  Suppressed = false
  Type = 0
FEATURE [Sketcher::SketchObject] Sketch305
  ArcFitTolerance = 1e-06
  AttachmentSupport = -> [Pad202]
  ExternalGeometry = -> [Pad202]
  FullyConstrained = true
  MakeInternals = false
  MapMode = 5
  Placement = pos=(7,-4e-16,0) rot=(0.57735,0.57735,0.57735;2.0944rad)
  sketch-geometry (4):
    g0: LineSegment StartX=10.35 StartY=-2 StartZ=0 EndX=3.05 EndY=-2 EndZ=0
    g1: LineSegment StartX=3.05 StartY=-2 StartZ=0 EndX=3.05 EndY=-10 EndZ=0
    g2: LineSegment StartX=3.05 StartY=-10 StartZ=0 EndX=10.35 EndY=-10 EndZ=0
    g3: LineSegment StartX=10.35 StartY=-10 StartZ=0 EndX=10.35 EndY=-2 EndZ=0
  constraints (11):
    c: Coincident(g0,g1)
    c: Coincident(g1,g2)
    c: Coincident(g2,g3)
    c: Coincident(g3,g0)
    c: Horizontal(g0)
    c: Horizontal(g2)
    c: Vertical(g1)
    c: Vertical(g3)
    c: DistanceX(g0,g0) = 7.3
    c: Coincident(g2,g-3)
    c: DistanceY(g1,g1) = 8
FEATURE [PartDesign::Pad] Pad203
  BaseFeature = -> Pad202
  Direction = (1,0,0)
  Length = 7
  Length2 = 10
  Profile = -> Sketch305
  ReferenceAxis = -> Sketch305 [N_Axis]
  Refine = true
  Reversed = true
  Suppressed = false
  Type = 0
FEATURE [PartDesign::Pocket] Pocket136
  BaseFeature = -> Pad203
  Direction = (0,-1,0)
  Length = 0.05
  Length2 = 5
  Profile = -> Pad203 [Face7]
  Refine = true
  Suppressed = false
  Type = 0
FEATURE [Sketcher::SketchObject] Sketch306
  ArcFitTolerance = 1e-06
  AttachmentSupport = -> [Pocket136]
  ExternalGeometry = -> [Pocket136]
  FullyConstrained = true
  MakeInternals = false
  MapMode = 5
  Placement = pos=(5,0,0) rot=(0.57735,-0.57735,-0.57735;2.0944rad)
  sketch-geometry (7):
    g0: ArcOfCircle CenterX=-33.95 CenterY=-7 CenterZ=0 NormalX=0 NormalY=0 NormalZ=1 AngleXU=0 Radius=5 StartAngle=3.78509 EndAngle=5.63968
    g1: ArcOfCircle CenterX=-20.75 CenterY=-7 CenterZ=0 NormalX=0 NormalY=0 NormalZ=1 AngleXU=0 Radius=5 StartAngle=3.78509 EndAngle=5.63968
    g2: LineSegment [constr] StartX=-10.3 StartY=-12 StartZ=0 EndX=-41.35 EndY=-12 EndZ=0
    g3: LineSegment [constr] StartX=-10.3 StartY=-12 StartZ=0 EndX=-10.3 EndY=-10 EndZ=0
    g4: LineSegment [constr] StartX=-41.35 StartY=-10 StartZ=0 EndX=-41.35 EndY=-12 EndZ=0
    g5: LineSegment StartX=-24.75 StartY=-10 StartZ=0 EndX=-16.75 EndY=-10 EndZ=0
    g6: LineSegment StartX=-37.95 StartY=-10 StartZ=0 EndX=-29.95 EndY=-10 EndZ=0
  constraints (22):
    c: PointOnObject(g0,g-3)
    c: PointOnObject(g1,g-3)
    c: PointOnObject(g1,g-3)
    c: Radius(g0) = 5
    c: Radius(g1) = 5
    c: Horizontal(g2)
    c: Tangent(g2,g0)
    c: Coincident(g3,g2)
    c: Coincident(g3,g-4)
    c: Vertical(g3)
    c: DistanceY(g3,g3) = 2
    c: Tangent(g1,g2)
    c: Coincident(g4,g-3)
    c: Coincident(g4,g2)
    c: Vertical(g4)
    c: PointOnObject(g0,g-3)
    c: DistanceX(g4,g0) = 3.4
    c: DistanceX(g0,g1) = 5.2
    c: Coincident(g5,g1)
    c: Coincident(g5,g1)
    c: Coincident(g6,g0)
    c: Coincident(g6,g0)
FEATURE [PartDesign::Pad] Pad204
  BaseFeature = -> Pocket136
  Direction = (-1,0,0)
  Length = 2
  Length2 = 10
  Profile = -> Sketch306
  ReferenceAxis = -> Sketch306 [N_Axis]
  Refine = true
  Reversed = true
  Suppressed = false
  Type = 0
FEATURE [Sketcher::SketchObject] Sketch307
  ArcFitTolerance = 1e-06
  AttachmentSupport = -> [Pad204]
  ExternalGeometry = -> [Pad204]
  FullyConstrained = true
  MakeInternals = false
  MapMode = 5
  Placement = pos=(5,0,0) rot=(0.57735,-0.57735,-0.57735;2.0944rad)
  sketch-geometry (6):
    g0: LineSegment StartX=-10.3 StartY=-10 StartZ=0 EndX=-12.05 EndY=-10 EndZ=0
    g1: LineSegment StartX=-12.05 StartY=-10 StartZ=0 EndX=-12.05 EndY=0 EndZ=0
    g2: LineSegment StartX=-12.05 StartY=0 StartZ=0 EndX=-10.35 EndY=0 EndZ=0
    g3: LineSegment StartX=-10.35 StartY=0 StartZ=0 EndX=-10.35 EndY=-2 EndZ=0
    g4: LineSegment StartX=-10.35 StartY=-2 StartZ=0 EndX=-10.3 EndY=-2 EndZ=0
    g5: LineSegment StartX=-10.3 StartY=-2 StartZ=0 EndX=-10.3 EndY=-10 EndZ=0
  constraints (14):
    c: Coincident(g0,g-5)
    c: PointOnObject(g0,g-5)
    c: DistanceX(g0,g0) = 1.75
    c: Coincident(g1,g0)
    c: PointOnObject(g1,g-6)
    c: Vertical(g1)
    c: Coincident(g2,g1)
    c: Coincident(g2,g-6)
    c: Coincident(g3,g2)
    c: Coincident(g3,g-4)
    c: Coincident(g4,g3)
    c: Coincident(g4,g-3)
    c: Coincident(g5,g4)
    c: Coincident(g5,g0)
FEATURE [PartDesign::Pad] Pad205
  BaseFeature = -> Pad204
  Direction = (-1,0,0)
  Length = 5
  Length2 = 10
  Profile = -> Sketch307
  ReferenceAxis = -> Sketch307 [N_Axis]
  Refine = true
  Suppressed = false
  Type = 0
FEATURE [Sketcher::SketchObject] Sketch308
  ArcFitTolerance = 1e-06
  AttachmentSupport = -> [Pad205]
  ExternalGeometry = -> [Pad205]
  FullyConstrained = true
  MakeInternals = false
  MapMode = 5
  Placement = pos=(5,0,0) rot=(0.57735,-0.57735,-0.57735;2.0944rad)
  sketch-geometry (3):
    g0: LineSegment StartX=-12.05 StartY=0 StartZ=0 EndX=-16.35 EndY=0 EndZ=0
    g1: LineSegment StartX=-16.35 StartY=0 StartZ=0 EndX=-12.05 EndY=-4.3 EndZ=0
    g2: LineSegment StartX=-12.05 StartY=-4.3 StartZ=0 EndX=-12.05 EndY=0 EndZ=0
  constraints (9):
    c: PointOnObject(g0,g-3)
    c: PointOnObject(g0,g-3)
    c: Coincident(g1,g0)
    c: PointOnObject(g1,g-4)
    c: Coincident(g2,g1)
    c: Coincident(g2,g0)
    c: Vertical(g2)
    c: DistanceX(g0,g0) = 4.3
    c: Angle(g1,g0) = 0.785398
FEATURE [PartDesign::Pad] Pad206
  BaseFeature = -> Pad205
  Direction = (-1,0,0)
  Length = 5
  Length2 = 10
  Profile = -> Sketch308
  ReferenceAxis = -> Sketch308 [N_Axis]
  Refine = true
  Suppressed = false
  Type = 0
FEATURE [Sketcher::SketchObject] Sketch309
  ArcFitTolerance = 1e-06
  AttachmentSupport = -> [Pad206]
  ExternalGeometry = -> [Pad206]
  FullyConstrained = true
  MakeInternals = false
  MapMode = 5
  Placement = pos=(5,0,0) rot=(0.57735,-0.57735,-0.57735;2.0944rad)
  sketch-geometry (3):
    g0: LineSegment StartX=-41.35 StartY=0 StartZ=0 EndX=-37.35 EndY=0 EndZ=0
    g1: LineSegment StartX=-37.35 StartY=0 StartZ=0 EndX=-41.35 EndY=-4 EndZ=0
    g2: LineSegment StartX=-41.35 StartY=-4 StartZ=0 EndX=-41.35 EndY=0 EndZ=0
  constraints (8):
    c: Coincident(g0,g-4)
    c: PointOnObject(g0,g-3)
    c: Coincident(g1,g0)
    c: Coincident(g2,g1)
    c: Coincident(g2,g0)
    c: Vertical(g2)
    c: DistanceY(g2,g2) = 4
    c: DistanceX(g0,g0) = 4
FEATURE [PartDesign::Pad] Pad207
  BaseFeature = -> Pad206
  Direction = (-1,0,0)
  Length = 5
  Length2 = 10
  Profile = -> Sketch309
  ReferenceAxis = -> Sketch309 [N_Axis]
  Refine = true
  Suppressed = false
  Type = 0
FEATURE [Sketcher::SketchObject] Sketch310
  ArcFitTolerance = 1e-06
  AttachmentSupport = -> [Pad207]
  ExternalGeometry = -> [Pad207]
  FullyConstrained = true
  MakeInternals = false
  MapMode = 5
  Placement = pos=(7,0,0) rot=(0.57735,0.57735,0.57735;2.0944rad)
  sketch-geometry (1):
    g0: Circle CenterX=30.35 CenterY=-4 CenterZ=0 NormalX=0 NormalY=0 NormalZ=1 AngleXU=0 Radius=4
  constraints (3):
    c: Diameter(g0) = 8
    c: Tangent(g0,g-3)
    c: DistanceX(g0,g-3) = 11
FEATURE [PartDesign::Pad] Pad208
  BaseFeature = -> Pad207
  Direction = (1,0,0)
  Length = 5
  Length2 = 10
  Profile = -> Sketch310
  ReferenceAxis = -> Sketch310 [N_Axis]
  Refine = true
  Suppressed = false
  Type = 0
FEATURE [Sketcher::SketchObject] Sketch311
  ArcFitTolerance = 1e-06
  AttachmentSupport = -> [Pad208]
  ExternalGeometry = -> [Pad208]
  FullyConstrained = true
  MakeInternals = false
  MapMode = 5
  Placement = pos=(5,0,0) rot=(0.57735,-0.57735,-0.57735;2.0944rad)
  sketch-geometry (1):
    g0: Circle CenterX=-30.35 CenterY=-4 CenterZ=0 NormalX=0 NormalY=0 NormalZ=1 AngleXU=0 Radius=2.1
  constraints (2):
    c: Coincident(g0,g-3)
    c: Diameter(g0) = 4.2
FEATURE [PartDesign::Pocket] Pocket137
  BaseFeature = -> Pad208
  Direction = (1,0,0)
  Length = 5
  Length2 = 5
  Profile = -> Sketch311
  ReferenceAxis = -> Sketch311 [N_Axis]
  Refine = true
  Suppressed = false
  Type = 0
FEATURE [Sketcher::SketchObject] Sketch312
  ArcFitTolerance = 1e-06
  AttachmentSupport = -> [Pocket137]
  ExternalGeometry = -> [Pocket137]
  FullyConstrained = true
  MakeInternals = false
  MapMode = 5
  Placement = pos=(12,0,0) rot=(0.57735,0.57735,0.57735;2.0944rad)
  sketch-geometry (1):
    g0: Circle CenterX=30.35 CenterY=-4 CenterZ=0 NormalX=0 NormalY=0 NormalZ=1 AngleXU=0 Radius=1.4
  constraints (2):
    c: Coincident(g0,g-3)
    c: Diameter(g0) = 2.8
FEATURE [PartDesign::Pocket] Pocket138
  BaseFeature = -> Pocket137
  Direction = (-1,0,0)
  Length = 5
  Length2 = 5
  Profile = -> Sketch312
  ReferenceAxis = -> Sketch312 [N_Axis]
  Refine = true
  Suppressed = false
  Type = 0
FEATURE [Sketcher::SketchObject] Sketch313
  ArcFitTolerance = 1e-06
  AttachmentSupport = -> [Pocket138]
  ExternalGeometry = -> [Pocket138]
  FullyConstrained = true
  MakeInternals = false
  MapMode = 5
  Placement = pos=(5,0,0) rot=(0.57735,-0.57735,-0.57735;2.0944rad)
  sketch-geometry (2):
    g0: Circle CenterX=-33.95 CenterY=-7 CenterZ=0 NormalX=0 NormalY=0 NormalZ=1 AngleXU=0 Radius=0.75
    g1: Circle CenterX=-20.75 CenterY=-7 CenterZ=0 NormalX=0 NormalY=0 NormalZ=1 AngleXU=0 Radius=0.75
  constraints (4):
    c: Coincident(g0,g-4)
    c: Coincident(g1,g-3)
    c: Radius(g0) = 0.75
    c: Radius(g1) = 0.75
FEATURE [PartDesign::Pocket] Pocket139
  BaseFeature = -> Pocket138
  Direction = (1,0,0)
  Length = 8
  Length2 = 5
  Profile = -> Sketch313
  ReferenceAxis = -> Sketch313 [N_Axis]
  Refine = true
  Suppressed = false
  Type = 0
FEATURE [Sketcher::SketchObject] Sketch314
  ArcFitTolerance = 1e-06
  AttachmentSupport = -> [Pocket139]
  ExternalGeometry = -> [Pocket139]
  FullyConstrained = true
  MakeInternals = false
  MapMode = 5
  Placement = pos=(0,0,-10) rot=(1,0,0;3.14159rad)
  sketch-geometry (1):
    g0: Circle CenterX=3.55 CenterY=-7.2 CenterZ=0 NormalX=0 NormalY=0 NormalZ=1 AngleXU=0 Radius=1.45
  constraints (3):
    c: Radius(g0) = 1.45
    c: DistanceX(g0,g-4) = 3.45
    c: DistanceY(g0,g-4) = 4.15
FEATURE [PartDesign::Pocket] Pocket140
  BaseFeature = -> Pocket139
  Direction = (0,0,1)
  Length = 6
  Length2 = 5
  Profile = -> Sketch314
  ReferenceAxis = -> Sketch314 [N_Axis]
  Refine = true
  Suppressed = false
  Type = 0
FEATURE [Sketcher::SketchObject] Sketch315
  ArcFitTolerance = 1e-06
  AttachmentSupport = -> [Pocket140]
  ExternalGeometry = -> [Pocket140]
  FullyConstrained = true
  MakeInternals = false
  MapMode = 5
  Placement = pos=(0,0,-10) rot=(1,0,0;3.14159rad)
  sketch-geometry (3):
    g0: LineSegment StartX=9e-16 StartY=-3.05 StartZ=0 EndX=1.5 EndY=-3.05 EndZ=0
    g1: LineSegment StartX=1.5 StartY=-3.05 StartZ=0 EndX=9e-16 EndY=-4.55 EndZ=0
    g2: LineSegment StartX=9e-16 StartY=-4.55 StartZ=0 EndX=9e-16 EndY=-3.05 EndZ=0
  constraints (8):
    c: Coincident(g0,g-4)
    c: PointOnObject(g0,g-3)
    c: Coincident(g1,g0)
    c: PointOnObject(g1,g-4)
    c: Coincident(g2,g1)
    c: Coincident(g2,g0)
    c: DistanceX(g0,g0) = 1.5
    c: DistanceY(g2,g2) = 1.5
FEATURE [PartDesign::Pocket] Pocket141
  BaseFeature = -> Pocket140
  Direction = (0,0,1)
  Length = 8
  Length2 = 5
  Profile = -> Sketch315
  ReferenceAxis = -> Sketch315 [N_Axis]
  Refine = true
  Suppressed = false
  Type = 0
FEATURE [Sketcher::SketchObject] Sketch316
  ArcFitTolerance = 1e-06
  AttachmentSupport = -> [Pocket141]
  ExternalGeometry = -> [Pocket141]
  FullyConstrained = true
  MakeInternals = false
  MapMode = 5
  Placement = pos=(7e-16,0,0) rot=(0.57735,-0.57735,-0.57735;2.0944rad)
  sketch-geometry (4):
    g0: LineSegment StartX=-7.15 StartY=-4.4 StartZ=0 EndX=-10.15 EndY=-4.4 EndZ=0
    g1: LineSegment StartX=-10.15 StartY=-4.4 StartZ=0 EndX=-10.15 EndY=-7.6 EndZ=0
    g2: LineSegment StartX=-10.15 StartY=-7.6 StartZ=0 EndX=-7.15 EndY=-7.6 EndZ=0
    g3: LineSegment StartX=-7.15 StartY=-7.6 StartZ=0 EndX=-7.15 EndY=-4.4 EndZ=0
  constraints (12):
    c: Coincident(g0,g1)
    c: Coincident(g1,g2)
    c: Coincident(g2,g3)
    c: Coincident(g3,g0)
    c: Horizontal(g0)
    c: Horizontal(g2)
    c: Vertical(g1)
    c: Vertical(g3)
    c: DistanceX(g0,g0) = 3
    c: DistanceY(g1,g1) = 3.2
    c: DistanceY(g-3,g2) = 2.4
    c: DistanceX(g-4,g1) = 1.9
FEATURE [PartDesign::Pocket] Pocket142
  BaseFeature = -> Pocket141
  Direction = (1,0,0)
  Length = 1.5
  Length2 = 5
  Profile = -> Sketch316
  ReferenceAxis = -> Sketch316 [N_Axis]
  Refine = true
  Suppressed = false
  Type = 0
FEATURE [Sketcher::SketchObject] Sketch317
  ArcFitTolerance = 1e-06
  AttachmentSupport = -> [Pocket142]
  ExternalGeometry = -> [Pocket142]
  FullyConstrained = true
  MakeInternals = false
  MapMode = 5
  Placement = pos=(2.275,2.275,0) rot=(0.862856,-0.357407,-0.357407;1.71777rad)
  sketch-geometry (12):
    g0: LineSegment StartX=-3.21734 StartY=-3.9 StartZ=0 EndX=-3.21734 EndY=-4.1 EndZ=0
    g1: LineSegment StartX=-3.21734 StartY=-4.1 StartZ=0 EndX=-1.09602 EndY=-4.1 EndZ=0
    g2: LineSegment StartX=-1.09602 StartY=-4.1 StartZ=0 EndX=-1.09602 EndY=-3.9 EndZ=0
    g3: LineSegment StartX=-1.09602 StartY=-3.9 StartZ=0 EndX=-3.21734 EndY=-3.9 EndZ=0
    g4: LineSegment StartX=-3.21734 StartY=-5.9 StartZ=0 EndX=-3.21734 EndY=-6.1 EndZ=0
    g5: LineSegment StartX=-3.21734 StartY=-6.1 StartZ=0 EndX=-1.09602 EndY=-6.1 EndZ=0
    g6: LineSegment StartX=-1.09602 StartY=-6.1 StartZ=0 EndX=-1.09602 EndY=-5.9 EndZ=0
    g7: LineSegment StartX=-1.09602 StartY=-5.9 StartZ=0 EndX=-3.21734 EndY=-5.9 EndZ=0
    g8: LineSegment StartX=-3.21734 StartY=-7.9 StartZ=0 EndX=-3.21734 EndY=-8.1 EndZ=0
    g9: LineSegment StartX=-3.21734 StartY=-8.1 StartZ=0 EndX=-1.09602 EndY=-8.1 EndZ=0
    g10: LineSegment StartX=-1.09602 StartY=-8.1 StartZ=0 EndX=-1.09602 EndY=-7.9 EndZ=0
    g11: LineSegment StartX=-1.09602 StartY=-7.9 StartZ=0 EndX=-3.21734 EndY=-7.9 EndZ=0
  constraints (36):
    c: Coincident(g0,g1)
    c: Coincident(g1,g2)
    c: Coincident(g2,g3)
    c: Coincident(g3,g0)
    c: Vertical(g0)
    c: Vertical(g2)
    c: Horizontal(g1)
    c: Horizontal(g3)
    c: PointOnObject(g0,g-5)
    c: PointOnObject(g1,g-3)
    c: Coincident(g4,g5)
    c: Coincident(g5,g6)
    c: Coincident(g6,g7)
    c: Coincident(g7,g4)
    c: Vertical(g4)
    c: Vertical(g6)
    c: Horizontal(g5)
    c: Horizontal(g7)
    c: PointOnObject(g4,g-5)
    c: Coincident(g8,g9)
    c: Coincident(g9,g10)
    c: Coincident(g10,g11)
    c: Coincident(g11,g8)
    c: Vertical(g8)
    c: Vertical(g10)
    c: Horizontal(g9)
    c: Horizontal(g11)
    c: PointOnObject(g8,g-5)
    c: PointOnObject(g9,g-3)
    c: DistanceY(g6,g6) = 0.2
    c: DistanceY(g10,g10) = 0.2
    c: DistanceY(g2,g2) = 0.2
    c: DistanceY(g6,g-4) = 3.9
    c: PointOnObject(g6,g-3)
    c: DistanceY(g6,g1) = 1.8
    c: DistanceY(g10,g5) = 1.8
FEATURE [PartDesign::Pocket] Pocket143
  BaseFeature = -> Pocket142
  Direction = (0.707107,0.707107,0)
  Length = 0.5
  Length2 = 5
  Profile = -> Sketch317
  ReferenceAxis = -> Sketch317 [N_Axis]
  Refine = true
  Suppressed = false
  Type = 0
FEATURE [Sketcher::SketchObject] Sketch318
  ArcFitTolerance = 1e-06
  AttachmentSupport = -> [Pocket143]
  ExternalGeometry = -> [Pocket143]
  FullyConstrained = true
  MakeInternals = false
  MapMode = 5
  Placement = pos=(0,3.05,0) rot=(1,0,0;1.5708rad)
  sketch-geometry (12):
    g0: LineSegment StartX=1.5 StartY=-3.9 StartZ=0 EndX=1.5 EndY=-4.1 EndZ=0
    g1: LineSegment StartX=1.5 StartY=-4.1 StartZ=0 EndX=7 EndY=-4.1 EndZ=0
    g2: LineSegment StartX=7 StartY=-4.1 StartZ=0 EndX=7 EndY=-3.9 EndZ=0
    g3: LineSegment StartX=7 StartY=-3.9 StartZ=0 EndX=1.5 EndY=-3.9 EndZ=0
    g4: LineSegment StartX=1.5 StartY=-5.9 StartZ=0 EndX=1.5 EndY=-6.1 EndZ=0
    g5: LineSegment StartX=1.5 StartY=-6.1 StartZ=0 EndX=7 EndY=-6.1 EndZ=0
    g6: LineSegment StartX=7 StartY=-6.1 StartZ=0 EndX=7 EndY=-5.9 EndZ=0
    g7: LineSegment StartX=7 StartY=-5.9 StartZ=0 EndX=1.5 EndY=-5.9 EndZ=0
    g8: LineSegment StartX=1.5 StartY=-7.9 StartZ=0 EndX=1.5 EndY=-8.1 EndZ=0
    g9: LineSegment StartX=1.5 StartY=-8.1 StartZ=0 EndX=7 EndY=-8.1 EndZ=0
    g10: LineSegment StartX=7 StartY=-8.1 StartZ=0 EndX=7 EndY=-7.9 EndZ=0
    g11: LineSegment StartX=7 StartY=-7.9 StartZ=0 EndX=1.5 EndY=-7.9 EndZ=0
  constraints (30):
    c: Coincident(g0,g1)
    c: Coincident(g1,g2)
    c: Coincident(g2,g3)
    c: Coincident(g3,g0)
    c: Vertical(g2)
    c: Horizontal(g1)
    c: Horizontal(g3)
    c: Coincident(g0,g-5)
    c: PointOnObject(g1,g-3)
    c: Coincident(g4,g5)
    c: Coincident(g5,g6)
    c: Coincident(g6,g7)
    c: Coincident(g7,g4)
    c: Vertical(g6)
    c: Horizontal(g5)
    c: Horizontal(g7)
    c: Coincident(g4,g-6)
    c: PointOnObject(g5,g-3)
    c: Coincident(g8,g9)
    c: Coincident(g9,g10)
    c: Coincident(g10,g11)
    c: Coincident(g11,g8)
    c: Vertical(g10)
    c: Horizontal(g9)
    c: Horizontal(g11)
    c: Coincident(g8,g-7)
    c: PointOnObject(g9,g-3)
    c: Coincident(g8,g-7)
    c: Coincident(g4,g-6)
    c: Coincident(g0,g-5)
FEATURE [PartDesign::Pocket] Pocket144
  BaseFeature = -> Pocket143
  Direction = (0,1,-2e-16)
  Length = 0.5
  Length2 = 5
  Profile = -> Sketch318
  ReferenceAxis = -> Sketch318 [N_Axis]
  Refine = true
  Suppressed = false
  Type = 0
FEATURE [Sketcher::SketchObject] Sketch319
  ArcFitTolerance = 1e-06
  AttachmentSupport = -> [Pocket144]
  ExternalGeometry = -> [Pocket144]
  FullyConstrained = true
  MakeInternals = false
  MapMode = 5
  Placement = pos=(7,0,0) rot=(0.57735,0.57735,0.57735;2.0944rad)
  sketch-geometry (12):
    g0: LineSegment StartX=3.05 StartY=-3.9 StartZ=0 EndX=3.05 EndY=-4.1 EndZ=0
    g1: LineSegment StartX=3.05 StartY=-4.1 StartZ=0 EndX=7.65 EndY=-4.1 EndZ=0
    g2: LineSegment StartX=7.65 StartY=-4.1 StartZ=0 EndX=7.65 EndY=-3.9 EndZ=0
    g3: LineSegment StartX=7.65 StartY=-3.9 StartZ=0 EndX=3.05 EndY=-3.9 EndZ=0
    g4: LineSegment StartX=3.05 StartY=-5.9 StartZ=0 EndX=3.05 EndY=-6.1 EndZ=0
    g5: LineSegment StartX=3.05 StartY=-6.1 StartZ=0 EndX=7.65 EndY=-6.1 EndZ=0
    g6: LineSegment StartX=7.65 StartY=-6.1 StartZ=0 EndX=7.65 EndY=-5.9 EndZ=0
    g7: LineSegment StartX=7.65 StartY=-5.9 StartZ=0 EndX=3.05 EndY=-5.9 EndZ=0
    g8: LineSegment StartX=7.65 StartY=-6.1 StartZ=0 EndX=7.85 EndY=-6.1 EndZ=0
    g9: LineSegment StartX=7.85 StartY=-6.1 StartZ=0 EndX=7.85 EndY=-2 EndZ=0
    g10: LineSegment StartX=7.85 StartY=-2 StartZ=0 EndX=7.65 EndY=-2 EndZ=0
    g11: LineSegment StartX=7.65 StartY=-2 StartZ=0 EndX=7.65 EndY=-6.1 EndZ=0
  constraints (31):
    c: Coincident(g0,g1)
    c: Coincident(g1,g2)
    c: Coincident(g2,g3)
    c: Coincident(g3,g0)
    c: Vertical(g2)
    c: Horizontal(g1)
    c: Horizontal(g3)
    c: Coincident(g0,g-4)
    c: Coincident(g4,g5)
    c: Coincident(g5,g6)
    c: Coincident(g6,g7)
    c: Coincident(g7,g4)
    c: Vertical(g6)
    c: Horizontal(g5)
    c: Horizontal(g7)
    c: Coincident(g4,g-7)
    c: Coincident(g0,g-7)
    c: Coincident(g4,g-8)
    c: DistanceX(g3,g3) = 4.6
    c: DistanceX(g7,g7) = 4.6
    c: Coincident(g8,g9)
    c: Coincident(g9,g10)
    c: Coincident(g10,g11)
    c: Coincident(g11,g8)
    c: Horizontal(g8)
    c: Horizontal(g10)
    c: Vertical(g9)
    c: Vertical(g11)
    c: Coincident(g8,g5)
    c: PointOnObject(g9,g-3)
    c: DistanceX(g8,g8) = 0.2
FEATURE [PartDesign::Pocket] Pocket145
  BaseFeature = -> Pocket144
  Direction = (-1,0,0)
  Length = 0.5
  Length2 = 5
  Profile = -> Sketch319
  ReferenceAxis = -> Sketch319 [N_Axis]
  Refine = true
  Suppressed = false
  Type = 0
FEATURE [Sketcher::SketchObject] Sketch320
  ArcFitTolerance = 1e-06
  AttachmentSupport = -> [Pocket145]
  ExternalGeometry = -> [Pocket145]
  FullyConstrained = true
  MakeInternals = false
  MapMode = 5
  Placement = pos=(7,0,0) rot=(0.57735,0.57735,0.57735;2.0944rad)
  sketch-geometry (12):
    g0: LineSegment StartX=7.85 StartY=-6.1 StartZ=0 EndX=7.95 EndY=-6.1 EndZ=0
    g1: LineSegment StartX=7.95 StartY=-6.1 StartZ=0 EndX=7.95 EndY=-5.9 EndZ=0
    g2: LineSegment StartX=7.95 StartY=-5.9 StartZ=0 EndX=7.85 EndY=-5.9 EndZ=0
    g3: LineSegment StartX=7.85 StartY=-5.9 StartZ=0 EndX=7.85 EndY=-6.1 EndZ=0
    g4: LineSegment StartX=6.25 StartY=-6.1 StartZ=0 EndX=6.05 EndY=-6.1 EndZ=0
    g5: LineSegment StartX=6.05 StartY=-6.1 StartZ=0 EndX=6.05 EndY=-10 EndZ=0
    g6: LineSegment StartX=6.05 StartY=-10 StartZ=0 EndX=6.25 EndY=-10 EndZ=0
    g7: LineSegment StartX=6.25 StartY=-10 StartZ=0 EndX=6.25 EndY=-6.1 EndZ=0
    g8: LineSegment StartX=3.55 StartY=-8.1 StartZ=0 EndX=6.05 EndY=-8.1 EndZ=0
    g9: LineSegment StartX=6.05 StartY=-8.1 StartZ=0 EndX=6.05 EndY=-7.9 EndZ=0
    g10: LineSegment StartX=6.05 StartY=-7.9 StartZ=0 EndX=3.55 EndY=-7.9 EndZ=0
    g11: LineSegment StartX=3.55 StartY=-7.9 StartZ=0 EndX=3.55 EndY=-8.1 EndZ=0
  constraints (33):
    c: Coincident(g0,g1)
    c: Coincident(g1,g2)
    c: Coincident(g2,g3)
    c: Coincident(g3,g0)
    c: Horizontal(g0)
    c: Horizontal(g2)
    c: Vertical(g1)
    c: Vertical(g3)
    c: Coincident(g0,g-4)
    c: Coincident(g4,g5)
    c: Coincident(g5,g6)
    c: Coincident(g6,g7)
    c: Coincident(g7,g4)
    c: Horizontal(g4)
    c: Horizontal(g6)
    c: Vertical(g5)
    c: Vertical(g7)
    c: PointOnObject(g4,g-3)
    c: PointOnObject(g5,g-5)
    c: DistanceX(g6,g6) = 0.2
    c: DistanceX(g4,g0) = 1.7
    c: Coincident(g8,g9)
    c: Coincident(g9,g10)
    c: Coincident(g10,g11)
    c: Coincident(g11,g8)
    c: Horizontal(g8)
    c: Horizontal(g10)
    c: Vertical(g9)
    c: Coincident(g8,g-6)
    c: PointOnObject(g9,g5)
    c: Coincident(g10,g-6)
    c: DistanceX(g-7,g8) = 3
    c: DistanceY(g1,g1) = 0.2
FEATURE [PartDesign::Pocket] Pocket146
  BaseFeature = -> Pocket145
  Direction = (-1,0,0)
  Length = 0.5
  Length2 = 5
  Profile = -> Sketch320
  ReferenceAxis = -> Sketch320 [N_Axis]
  Refine = true
  Suppressed = false
  Type = 0
FEATURE [Sketcher::SketchObject] Sketch321
  ArcFitTolerance = 1e-06
  AttachmentSupport = -> [Pocket146]
  ExternalGeometry = -> [Pocket146]
  FullyConstrained = true
  MakeInternals = false
  MapMode = 5
  Placement = pos=(7,0,0) rot=(0.57735,0.57735,0.57735;2.0944rad)
  sketch-geometry (12):
    g0: LineSegment StartX=7.95 StartY=-5.9 StartZ=0 EndX=7.95 EndY=-8.1 EndZ=0
    g1: LineSegment StartX=7.95 StartY=-8.1 StartZ=0 EndX=8.15 EndY=-8.1 EndZ=0
    g2: LineSegment StartX=8.15 StartY=-8.1 StartZ=0 EndX=8.15 EndY=-5.9 EndZ=0
    g3: LineSegment StartX=8.15 StartY=-5.9 StartZ=0 EndX=7.95 EndY=-5.9 EndZ=0
    g4: LineSegment StartX=10.35 StartY=-2 StartZ=0 EndX=11.85 EndY=-2 EndZ=0
    g5: LineSegment StartX=11.85 StartY=-2 StartZ=0 EndX=11.85 EndY=-1.8 EndZ=0
    g6: LineSegment StartX=11.85 StartY=-1.8 StartZ=0 EndX=10.35 EndY=-1.8 EndZ=0
    g7: LineSegment StartX=10.35 StartY=-1.8 StartZ=0 EndX=10.35 EndY=-2 EndZ=0
    g8: LineSegment StartX=11.85 StartY=-1.8 StartZ=0 EndX=11.85 EndY=-10 EndZ=0
    g9: LineSegment StartX=11.85 StartY=-10 StartZ=0 EndX=12.05 EndY=-10 EndZ=0
    g10: LineSegment StartX=12.05 StartY=-10 StartZ=0 EndX=12.05 EndY=-1.8 EndZ=0
    g11: LineSegment StartX=12.05 StartY=-1.8 StartZ=0 EndX=11.85 EndY=-1.8 EndZ=0
  constraints (33):
    c: Coincident(g0,g1)
    c: Coincident(g1,g2)
    c: Coincident(g2,g3)
    c: Coincident(g3,g0)
    c: Vertical(g0)
    c: Vertical(g2)
    c: Horizontal(g1)
    c: Horizontal(g3)
    c: Coincident(g0,g-3)
    c: DistanceY(g0,g-4) = 0
    c: DistanceX(g3,g3) = 0.2
    c: Coincident(g4,g5)
    c: Coincident(g5,g6)
    c: Coincident(g6,g7)
    c: Coincident(g7,g4)
    c: Horizontal(g4)
    c: Horizontal(g6)
    c: Vertical(g5)
    c: Vertical(g7)
    c: Coincident(g4,g-5)
    c: Coincident(g8,g9)
    c: Coincident(g9,g10)
    c: Coincident(g10,g11)
    c: Coincident(g11,g8)
    c: Vertical(g8)
    c: Vertical(g10)
    c: Horizontal(g9)
    c: Horizontal(g11)
    c: Coincident(g8,g5)
    c: PointOnObject(g8,g-6)
    c: DistanceX(g9,g9) = 0.2
    c: DistanceY(g7,g7) = 0.2
    c: DistanceX(g-7,g4) = 4
FEATURE [PartDesign::Pocket] Pocket147
  BaseFeature = -> Pocket146
  Direction = (-1,0,0)
  Length = 0.5
  Length2 = 5
  Profile = -> Sketch321
  ReferenceAxis = -> Sketch321 [N_Axis]
  Refine = true
  Suppressed = false
  Type = 0
FEATURE [Sketcher::SketchObject] Sketch322
  ArcFitTolerance = 1e-06
  AttachmentSupport = -> [Pocket147]
  ExternalGeometry = -> [Pocket147]
  FullyConstrained = true
  MakeInternals = false
  MapMode = 5
  Placement = pos=(7,0,0) rot=(0.57735,0.57735,0.57735;2.0944rad)
  sketch-geometry (7):
    g0: LineSegment StartX=11.85 StartY=-6.31716 StartZ=0 EndX=11.85 EndY=-6.11716 EndZ=0
    g1: LineSegment StartX=11.85 StartY=-6.11716 StartZ=0 EndX=9.85 EndY=-6.11716 EndZ=0
    g2: LineSegment StartX=9.93284 StartY=-6.31716 StartZ=0 EndX=11.85 EndY=-6.31716 EndZ=0
    g3: LineSegment StartX=8.15 StartY=-8.1 StartZ=0 EndX=9.93284 EndY=-6.31716 EndZ=0
    g4: LineSegment StartX=9.85 StartY=-6.11716 StartZ=0 EndX=8.15 EndY=-7.81716 EndZ=0
    g5: LineSegment StartX=8.15 StartY=-7.81716 StartZ=0 EndX=8.15 EndY=-8.1 EndZ=0
    g6: LineSegment [constr] StartX=8.85711 StartY=-7.11005 StartZ=0 EndX=8.99853 EndY=-7.25147 EndZ=0
  constraints (21):
    c: Coincident(g0,g1)
    c: Coincident(g2,g0)
    c: Vertical(g0)
    c: Horizontal(g1)
    c: Horizontal(g2)
    c: PointOnObject(g0,g-4)
    c: DistanceY(g2,g1) = 0.2
    c: DistanceX(g1,g1) = 2
    c: Coincident(g3,g-3)
    c: Coincident(g4,g1)
    c: PointOnObject(g4,g-3)
    c: Coincident(g5,g4)
    c: Coincident(g5,g3)
    c: Coincident(g3,g2)
    c: Parallel(g4,g3)
    c: Angle(g4,g-3) = 0.785398
    c: PointOnObject(g6,g4)
    c: PointOnObject(g6,g3)
    c: Angle(g4,g6) = 1.5708
    c: Distance(g6,g4) = 1
    c: Distance(g6) = 0.2
FEATURE [PartDesign::Pocket] Pocket148
  BaseFeature = -> Pocket147
  Direction = (-1,0,0)
  Length = 0.5
  Length2 = 5
  Profile = -> Sketch322
  ReferenceAxis = -> Sketch322 [N_Axis]
  Refine = true
  Suppressed = false
  Type = 0
FEATURE [Sketcher::SketchObject] Sketch323
  ArcFitTolerance = 1e-06
  AttachmentSupport = -> [Pocket148]
  ExternalGeometry = -> [Pocket148]
  FullyConstrained = true
  MakeInternals = false
  MapMode = 5
  Placement = pos=(7e-16,0,0) rot=(0.57735,-0.57735,-0.57735;2.0944rad)
  sketch-geometry (1):
    g0: Circle CenterX=-11.85 CenterY=-2.5 CenterZ=0 NormalX=0 NormalY=0 NormalZ=1 AngleXU=0 Radius=1
  constraints (3):
    c: Diameter(g0) = 2
    c: DistanceX(g0,g-3) = 1.5
    c: DistanceY(g0,g-3) = 0.5
FEATURE [PartDesign::Pocket] Pocket149
  BaseFeature = -> Pocket148
  Direction = (1,0,0)
  Length = 0.5
  Length2 = 5
  Profile = -> Sketch323
  ReferenceAxis = -> Sketch323 [N_Axis]
  Refine = true
  Suppressed = false
  Type = 0
FEATURE [PartDesign::Body] Body021  label="Pre_Right_Arm"
  AllowCompound = false
  Group = -> [Binder015,Sketch304,Pad202,Sketch305,Pad203,Pocket136,Sketch306,Pad204,Sketch307,Pad205,Sketch308,Pad206,Sketch309,Pad207,Sketch310,Pad208,Sketch311,Pocket137,Sketch312,Pocket138,Sketch313,Pocket139,Sketch314,Pocket140,Sketch315,Pocket141,Sketch316,Pocket142,Sketch317,Pocket143,Sketch318,Pocket144,Sketch319,Pocket145,Sketch320,Pocket146,Sketch321,Pocket147,Sketch322,Pocket148,Sketch323,Pocket149,+4 more]
  Origin = -> Origin022
  Tip = -> Pocket150
COMPONENT P20 — recipe-attached ("Pre_Right_Shoulder", modeled in this document).
Construction recipe (the document's own serialized feature program — sketch geometry with constraints, then the solid features built on it; lengths are millimeters unless a unit is written):

FEATURE [PartDesign::SubShapeBinder] Binder016
  BindCopyOnChange = 0
  BindMode = 2
  ClaimChildren = false
  Context = -> Body022 [Binder016.]
  Fuse = false
  MakeFace = true
  OffsetFill = false
  OffsetIntersection = false
  OffsetJoinType = 0
  OffsetOpenResult = false
  PartialLoad = false
  Refine = true
  Relative = true
  _Version = 2
FEATURE [Sketcher::SketchObject] Sketch325
  ArcFitTolerance = 1e-06
  AttachmentSupport = -> [Binder016]
  ExternalGeometry = -> [Binder016]
  FullyConstrained = true
  MakeInternals = false
  MapMode = 5
  Placement = pos=(12,0,0) rot=(0.57735,0.57735,0.57735;2.0944rad)
  sketch-geometry (4):
    g0: LineSegment StartX=26.35 StartY=-0.05 StartZ=0 EndX=26.35 EndY=-7.25 EndZ=0
    g1: LineSegment StartX=26.35 StartY=-7.25 StartZ=0 EndX=34.35 EndY=-7.25 EndZ=0
    g2: LineSegment StartX=34.35 StartY=-7.25 StartZ=0 EndX=34.35 EndY=-0.05 EndZ=0
    g3: LineSegment StartX=34.35 StartY=-0.05 StartZ=0 EndX=26.35 EndY=-0.05 EndZ=0
  constraints (12):
    c: Coincident(g0,g1)
    c: Coincident(g1,g2)
    c: Coincident(g2,g3)
    c: Coincident(g3,g0)
    c: Vertical(g0)
    c: Vertical(g2)
    c: Horizontal(g1)
    c: Horizontal(g3)
    c: DistanceX(g3,g3) = 8
    c: DistanceY(g0,g0) = 7.2
    c: DistanceX(g0,g-3) = 4
    c: DistanceY(g-3,g0) = 3.95
FEATURE [PartDesign::Pad] Pad210
  Direction = (1,0,0)
  Length = 5.3
  Length2 = 10
  Profile = -> Sketch325
  ReferenceAxis = -> Sketch325 [N_Axis]
  Refine = true
  Suppressed = false
  Type = 0
FEATURE [Sketcher::SketchObject] Sketch326
  ArcFitTolerance = 1e-06
  AttachmentSupport = -> [Pad210]
  ExternalGeometry = -> [Binder016]
  FullyConstrained = true
  MakeInternals = false
  MapMode = 5
  Placement = pos=(12,0,0) rot=(0.57735,-0.57735,-0.57735;2.0944rad)
  sketch-geometry (1):
    g0: Circle CenterX=-30.35 CenterY=-4 CenterZ=0 NormalX=0 NormalY=0 NormalZ=1 AngleXU=0 Radius=0.9
  constraints (2):
    c: Coincident(g0,g-3)
    c: Radius(g0) = 0.9
FEATURE [PartDesign::Pocket] Pocket151
  BaseFeature = -> Pad210
  Direction = (1,0,0)
  Length = 7
  Length2 = 5
  Profile = -> Sketch326
  ReferenceAxis = -> Sketch326 [N_Axis]
  Refine = true
  Suppressed = false
  Type = 0
FEATURE [Sketcher::SketchObject] Sketch327
  ArcFitTolerance = 1e-06
  AttachmentSupport = -> [Pocket151]
  ExternalGeometry = -> [Pocket151]
  FullyConstrained = true
  MakeInternals = false
  MapMode = 5
  Placement = pos=(0,34.35,0) rot=(0,0.707107,0.707107;3.14159rad)
  sketch-geometry (4):
    g0: LineSegment StartX=-17.3 StartY=-0.05 StartZ=0 EndX=-17.3 EndY=-7.25 EndZ=0
    g1: LineSegment StartX=-17.3 StartY=-7.25 StartZ=0 EndX=-16.3 EndY=-7.25 EndZ=0
    g2: LineSegment StartX=-16.3 StartY=-7.25 StartZ=0 EndX=-16.3 EndY=-0.05 EndZ=0
    g3: LineSegment StartX=-16.3 StartY=-0.05 StartZ=0 EndX=-17.3 EndY=-0.05 EndZ=0
  constraints (11):
    c: Coincident(g0,g1)
    c: Coincident(g1,g2)
    c: Coincident(g2,g3)
    c: Coincident(g3,g0)
    c: Vertical(g0)
    c: Vertical(g2)
    c: Horizontal(g1)
    c: Horizontal(g3)
    c: Coincident(g0,g-5)
    c: PointOnObject(g1,g-4)
    c: DistanceX(g1,g1) = 1
FEATURE [PartDesign::Pad] Pad211
  BaseFeature = -> Pocket151
  Direction = (0,1,-2e-16)
  Length = 1.2
  Length2 = 10
  Profile = -> Sketch327
  ReferenceAxis = -> Sketch327 [N_Axis]
  Refine = true
  Suppressed = false
  Type = 0
FEATURE [Sketcher::SketchObject] Sketch328
  ArcFitTolerance = 1e-06
  AttachmentSupport = -> [Pad211]
  ExternalGeometry = -> [Pad211]
  FullyConstrained = true
  MakeInternals = false
  MapMode = 5
  Placement = pos=(0,26.35,0) rot=(1,0,0;1.5708rad)
  sketch-geometry (4):
    g0: LineSegment StartX=17.3 StartY=-0.05 StartZ=0 EndX=16.3 EndY=-0.05 EndZ=0
    g1: LineSegment StartX=16.3 StartY=-0.05 StartZ=0 EndX=16.3 EndY=-7.25 EndZ=0
    g2: LineSegment StartX=16.3 StartY=-7.25 StartZ=0 EndX=17.3 EndY=-7.25 EndZ=0
    g3: LineSegment StartX=17.3 StartY=-7.25 StartZ=0 EndX=17.3 EndY=-0.05 EndZ=0
  constraints (11):
    c: Coincident(g0,g1)
    c: Coincident(g1,g2)
    c: Coincident(g2,g3)
    c: Coincident(g3,g0)
    c: Horizontal(g0)
    c: Horizontal(g2)
    c: Vertical(g1)
    c: Vertical(g3)
    c: Coincident(g0,g-3)
    c: PointOnObject(g1,g-4)
    c: DistanceX(g2,g2) = 1
FEATURE [PartDesign::Pad] Pad212
  BaseFeature = -> Pad211
  Direction = (0,-1,2e-16)
  Length = 1.2
  Length2 = 10
  Profile = -> Sketch328
  ReferenceAxis = -> Sketch328 [N_Axis]
  Refine = true
  Suppressed = false
  Type = 0
FEATURE [PartDesign::Pad] Pad244
  BaseFeature = -> Pad212
  Direction = (3e-16,0,-1)
  Length = 0.1
  Length2 = 10
  Profile = -> Pad212 [Face9]
  Refine = true
  Suppressed = false
  Type = 0
FEATURE [PartDesign::Pad] Pad245
  BaseFeature = -> Pad244
  Direction = (0,0,1)
  Length = 0.05
  Length2 = 10
  Profile = -> Pad244 [Face3]
  Refine = true
  Suppressed = false
  Type = 0
FEATURE [Sketcher::SketchObject] Sketch355
  ArcFitTolerance = 1e-06
  AttachmentSupport = -> [Pad245]
  ExternalGeometry = -> [Pad245]
  FullyConstrained = true
  MakeInternals = false
  MapMode = 5
  Placement = pos=(2.1e-15,0,-7.35) rot=(1,0,0;3.14159rad)
  sketch-geometry (12):
    g0: LineSegment StartX=12 StartY=-28.3 StartZ=0 EndX=12 EndY=-32.4 EndZ=0
    g1: LineSegment StartX=12 StartY=-32.4 StartZ=0 EndX=17.3 EndY=-32.4 EndZ=0
    g2: LineSegment StartX=17.3 StartY=-32.4 StartZ=0 EndX=17.3 EndY=-28.3 EndZ=0
    g3: LineSegment StartX=17.3 StartY=-28.3 StartZ=0 EndX=12 EndY=-28.3 EndZ=0
    g4: LineSegment StartX=16.3 StartY=-25.15 StartZ=0 EndX=16.3 EndY=-26.3 EndZ=0
    g5: LineSegment StartX=16.3 StartY=-26.3 StartZ=0 EndX=17.3 EndY=-26.3 EndZ=0
    g6: LineSegment StartX=17.3 StartY=-26.3 StartZ=0 EndX=17.3 EndY=-25.15 EndZ=0
    g7: LineSegment StartX=17.3 StartY=-25.15 StartZ=0 EndX=16.3 EndY=-25.15 EndZ=0
    g8: LineSegment StartX=16.3 StartY=-35.55 StartZ=0 EndX=17.3 EndY=-35.55 EndZ=0
    g9: LineSegment StartX=17.3 StartY=-35.55 StartZ=0 EndX=17.3 EndY=-34.4 EndZ=0
    g10: LineSegment StartX=17.3 StartY=-34.4 StartZ=0 EndX=16.3 EndY=-34.4 EndZ=0
    g11: LineSegment StartX=16.3 StartY=-34.4 StartZ=0 EndX=16.3 EndY=-35.55 EndZ=0
  constraints (34):
    c: Coincident(g0,g1)
    c: Coincident(g1,g2)
    c: Coincident(g2,g3)
    c: Coincident(g3,g0)
    c: Vertical(g0)
    c: Vertical(g2)
    c: Horizontal(g1)
    c: Horizontal(g3)
    c: PointOnObject(g0,g-10)
    c: PointOnObject(g1,g-6)
    c: Coincident(g4,g5)
    c: Coincident(g5,g6)
    c: Coincident(g6,g7)
    c: Coincident(g7,g4)
    c: Vertical(g4)
    c: Vertical(g6)
    c: Horizontal(g5)
    c: Horizontal(g7)
    c: Coincident(g4,g-4)
    c: PointOnObject(g5,g-6)
    c: Coincident(g8,g9)
    c: Coincident(g9,g10)
    c: Coincident(g10,g11)
    c: Coincident(g11,g8)
    c: Horizontal(g8)
    c: Horizontal(g10)
    c: Vertical(g9)
    c: Vertical(g11)
    c: Coincident(g8,g-8)
    c: PointOnObject(g9,g-6)
    c: DistanceY(g11,g11) = 1.15
    c: DistanceY(g4,g4) = 1.15
    c: DistanceY(g2,g5) = 2
    c: DistanceY(g9,g1) = 2
FEATURE [PartDesign::Pad] Pad255
  BaseFeature = -> Pad245
  Direction = (0,0,-1)
  Length = 0.6
  Length2 = 10
  Profile = -> Sketch355
  ReferenceAxis = -> Sketch355 [N_Axis]
  Refine = true
  Suppressed = false
  Type = 0
FEATURE [PartDesign::Body] Body022  label="Pre_Right_Shoulder"
  AllowCompound = false
  Group = -> [Binder016,Sketch325,Pad210,Sketch326,Pocket151,Sketch327,Pad211,Sketch328,Pad212,Pad244,Pad245,Sketch355,Pad255]
  Origin = -> Origin023
  Tip = -> Pad255
COMPONENT P21 — recipe-attached ("Tire2", modeled in this document).
Construction recipe (the document's own serialized feature program — sketch geometry with constraints, then the solid features built on it; lengths are millimeters unless a unit is written):

FEATURE [Sketcher::SketchObject] Sketch329
  ArcFitTolerance = 1e-06
  AttachmentSupport = -> [XY_Plane024]
  FullyConstrained = true
  MakeInternals = false
  MapMode = 5
  sketch-geometry (1):
    g0: Circle CenterX=0 CenterY=0 CenterZ=0 NormalX=0 NormalY=0 NormalZ=1 AngleXU=0 Radius=6.05
  constraints (2):
    c: Coincident(g0,g-1)
    c: Diameter(g0) = 12.1
FEATURE [PartDesign::Pad] Pad213
  Direction = (0,0,1)
  Length = 3.6
  Length2 = 10
  Profile = -> Sketch329
  ReferenceAxis = -> Sketch329 [N_Axis]
  Refine = true
  Suppressed = false
  Type = 0
FEATURE [Sketcher::SketchObject] Sketch330
  ArcFitTolerance = 1e-06
  AttachmentSupport = -> [Pad213]
  FullyConstrained = true
  MakeInternals = false
  MapMode = 5
  Placement = pos=(0,0,3.6) rot=(0,0,1;0rad)
  sketch-geometry (1):
    g0: Circle CenterX=0 CenterY=0 CenterZ=0 NormalX=0 NormalY=0 NormalZ=1 AngleXU=0 Radius=3.55
  constraints (2):
    c: Coincident(g0,g-1)
    c: Diameter(g0) = 7.1
FEATURE [PartDesign::Pad] Pad214
  BaseFeature = -> Pad213
  Direction = (0,0,1)
  Length = 0.5
  Length2 = 10
  Profile = -> Sketch330
  ReferenceAxis = -> Sketch330 [N_Axis]
  Refine = true
  Suppressed = false
  Type = 0
FEATURE [Sketcher::SketchObject] Sketch331
  ArcFitTolerance = 1e-06
  AttachmentSupport = -> [Pad214]
  ExternalGeometry = -> [Pad214]
  FullyConstrained = true
  MakeInternals = false
  MapMode = 5
  Placement = pos=(0,0,3.6) rot=(0,0,1;0rad)
  sketch-geometry (2):
    g0: Circle CenterX=0 CenterY=0 CenterZ=0 NormalX=0 NormalY=0 NormalZ=1 AngleXU=0 Radius=5
    g1: Circle CenterX=0 CenterY=0 CenterZ=0 NormalX=0 NormalY=0 NormalZ=1 AngleXU=0 Radius=6.05
  constraints (5):
    c: Diameter(g0) = 10
    c: Coincident(g1,g0)
    c: Diameter(g-3) = 12.1
    c: Diameter(g1) = 12.1
    c: Coincident(g0,g-1)
FEATURE [PartDesign::Pocket] Pocket152
  BaseFeature = -> Pad214
  Direction = (0,0,-1)
  Length = 1
  Length2 = 5
  Profile = -> Sketch331
  ReferenceAxis = -> Sketch331 [N_Axis]
  Refine = true
  Suppressed = false
  Type = 0
FEATURE [Sketcher::SketchObject] Sketch332
  ArcFitTolerance = 1e-06
  AttachmentSupport = -> [Pocket152]
  ExternalGeometry = -> [Pocket152]
  FullyConstrained = true
  MakeInternals = false
  MapMode = 5
  Placement = pos=(0,0,3.6) rot=(0,0,1;0rad)
  sketch-geometry (50):
    g0: Circle [constr] CenterX=0 CenterY=0 CenterZ=0 NormalX=0 NormalY=0 NormalZ=1 AngleXU=0 Radius=6.05
    g1: LineSegment StartX=4e-16 StartY=6.05 StartZ=0 EndX=-0.789683 EndY=5.99824 EndZ=0
    g2: LineSegment StartX=-0.789683 StartY=5.99824 StartZ=0 EndX=-1.56586 EndY=5.84385 EndZ=0
    g3: LineSegment StartX=-1.56586 StartY=5.84385 StartZ=0 EndX=-2.31523 EndY=5.58947 EndZ=0
    g4: LineSegment StartX=-2.31523 StartY=5.58947 StartZ=0 EndX=-3.025 EndY=5.23945 EndZ=0
    g5: LineSegment StartX=-3.025 StartY=5.23945 StartZ=0 EndX=-3.68301 EndY=4.79979 EndZ=0
    g6: LineSegment StartX=-3.68301 StartY=4.79979 StartZ=0 EndX=-4.278 EndY=4.278 EndZ=0
    g7: LineSegment StartX=-4.278 StartY=4.278 StartZ=0 EndX=-4.79979 EndY=3.68301 EndZ=0
    g8: LineSegment StartX=-4.79979 StartY=3.68301 StartZ=0 EndX=-5.23945 EndY=3.025 EndZ=0
    g9: LineSegment StartX=-5.23945 StartY=3.025 StartZ=0 EndX=-5.58947 EndY=2.31523 EndZ=0
    g10: LineSegment StartX=-5.58947 StartY=2.31523 StartZ=0 EndX=-5.84385 EndY=1.56586 EndZ=0
    g11: LineSegment StartX=-5.84385 StartY=1.56586 StartZ=0 EndX=-5.99824 EndY=0.789683 EndZ=0
    g12: LineSegment StartX=-5.99824 StartY=0.789683 StartZ=0 EndX=-6.05 EndY=4e-16 EndZ=0
    g13: LineSegment StartX=-6.05 StartY=4e-16 StartZ=0 EndX=-5.99824 EndY=-0.789683 EndZ=0
    g14: LineSegment StartX=-5.99824 StartY=-0.789683 StartZ=0 EndX=-5.84385 EndY=-1.56586 EndZ=0
    g15: LineSegment StartX=-5.84385 StartY=-1.56586 StartZ=0 EndX=-5.58947 EndY=-2.31523 EndZ=0
    g16: LineSegment StartX=-5.58947 StartY=-2.31523 StartZ=0 EndX=-5.23945 EndY=-3.025 EndZ=0
    g17: LineSegment StartX=-5.23945 StartY=-3.025 StartZ=0 EndX=-4.79979 EndY=-3.68301 EndZ=0
    g18: LineSegment StartX=-4.79979 StartY=-3.68301 StartZ=0 EndX=-4.278 EndY=-4.278 EndZ=0
    g19: LineSegment StartX=-4.278 StartY=-4.278 StartZ=0 EndX=-3.68301 EndY=-4.79979 EndZ=0
    g20: LineSegment StartX=-3.68301 StartY=-4.79979 StartZ=0 EndX=-3.025 EndY=-5.23945 EndZ=0
    g21: LineSegment StartX=-3.025 StartY=-5.23945 StartZ=0 EndX=-2.31523 EndY=-5.58947 EndZ=0
    g22: LineSegment StartX=-2.31523 StartY=-5.58947 StartZ=0 EndX=-1.56586 EndY=-5.84385 EndZ=0
    g23: LineSegment StartX=-1.56586 StartY=-5.84385 StartZ=0 EndX=-0.789683 EndY=-5.99824 EndZ=0
    g24: LineSegment StartX=-0.789683 StartY=-5.99824 StartZ=0 EndX=-1e-16 EndY=-6.05 EndZ=0
    g25: LineSegment StartX=-1e-16 StartY=-6.05 StartZ=0 EndX=0.789683 EndY=-5.99824 EndZ=0
    g26: LineSegment StartX=0.789683 StartY=-5.99824 StartZ=0 EndX=1.56586 EndY=-5.84385 EndZ=0
    g27: LineSegment StartX=1.56586 StartY=-5.84385 StartZ=0 EndX=2.31523 EndY=-5.58947 EndZ=0
    g28: LineSegment StartX=2.31523 StartY=-5.58947 StartZ=0 EndX=3.025 EndY=-5.23945 EndZ=0
    g29: LineSegment StartX=3.025 StartY=-5.23945 StartZ=0 EndX=3.68301 EndY=-4.79979 EndZ=0
    g30: LineSegment StartX=3.68301 StartY=-4.79979 StartZ=0 EndX=4.278 EndY=-4.278 EndZ=0
    g31: LineSegment StartX=4.278 StartY=-4.278 StartZ=0 EndX=4.79979 EndY=-3.68301 EndZ=0
    g32: LineSegment StartX=4.79979 StartY=-3.68301 StartZ=0 EndX=5.23945 EndY=-3.025 EndZ=0
    g33: LineSegment StartX=5.23945 StartY=-3.025 StartZ=0 EndX=5.58947 EndY=-2.31523 EndZ=0
    g34: LineSegment StartX=5.58947 StartY=-2.31523 StartZ=0 EndX=5.84385 EndY=-1.56586 EndZ=0
    g35: LineSegment StartX=5.84385 StartY=-1.56586 StartZ=0 EndX=5.99824 EndY=-0.789683 EndZ=0
    g36: LineSegment StartX=5.99824 StartY=-0.789683 StartZ=0 EndX=6.05 EndY=0 EndZ=0
    g37: LineSegment StartX=6.05 StartY=0 StartZ=0 EndX=5.99824 EndY=0.789683 EndZ=0
    g38: LineSegment StartX=5.99824 StartY=0.789683 StartZ=0 EndX=5.84385 EndY=1.56586 EndZ=0
    g39: LineSegment StartX=5.84385 StartY=1.56586 StartZ=0 EndX=5.58947 EndY=2.31523 EndZ=0
    g40: LineSegment StartX=5.58947 StartY=2.31523 StartZ=0 EndX=5.23945 EndY=3.025 EndZ=0
    g41: LineSegment StartX=5.23945 StartY=3.025 StartZ=0 EndX=4.79979 EndY=3.68301 EndZ=0
    g42: LineSegment StartX=4.79979 StartY=3.68301 StartZ=0 EndX=4.278 EndY=4.278 EndZ=0
    g43: LineSegment StartX=4.278 StartY=4.278 StartZ=0 EndX=3.68301 EndY=4.79979 EndZ=0
    g44: LineSegment StartX=3.68301 StartY=4.79979 StartZ=0 EndX=3.025 EndY=5.23945 EndZ=0
    g45: LineSegment StartX=3.025 StartY=5.23945 StartZ=0 EndX=2.31523 EndY=5.58947 EndZ=0
    g46: LineSegment StartX=2.31523 StartY=5.58947 StartZ=0 EndX=1.56586 EndY=5.84385 EndZ=0
    g47: LineSegment StartX=1.56586 StartY=5.84385 StartZ=0 EndX=0.789683 EndY=5.99824 EndZ=0
    g48: LineSegment StartX=0.789683 StartY=5.99824 StartZ=0 EndX=4e-16 EndY=6.05 EndZ=0
    g49: Circle [constr] CenterX=0 CenterY=0 CenterZ=0 NormalX=0 NormalY=0 NormalZ=1 AngleXU=0 Radius=6.05
  constraints (102):
    c: Coincident(g0,g-1)
    c: Coincident(g1,g2)
    c: Coincident(g2,g3)
    c: Coincident(g3,g4)
    c: Coincident(g4,g5)
    c: Coincident(g5,g6)
    c: Coincident(g6,g7)
    c: Coincident(g7,g8)
    c: Coincident(g8,g9)
    c: Coincident(g9,g10)
    c: Coincident(g10,g11)
    c: Coincident(g11,g12)
    c: Coincident(g12,g13)
    c: Coincident(g13,g14)
    c: Coincident(g14,g15)
    c: Coincident(g15,g16)
    c: Coincident(g16,g17)
    c: Coincident(g17,g18)
    c: Coincident(g18,g19)
    c: Coincident(g19,g20)
    c: Coincident(g20,g21)
    c: Coincident(g21,g22)
    c: Coincident(g22,g23)
    c: Coincident(g23,g24)
    c: Coincident(g24,g25)
    c: Coincident(g25,g26)
    c: Coincident(g26,g27)
    c: Coincident(g27,g28)
    c: Coincident(g28,g29)
    c: Coincident(g29,g30)
    c: Coincident(g30,g31)
    c: Coincident(g31,g32)
    c: Coincident(g32,g33)
    c: Coincident(g33,g34)
    c: Coincident(g34,g35)
    c: Coincident(g35,g36)
    c: Coincident(g36,g37)
    c: Coincident(g37,g38)
    c: Coincident(g38,g39)
    c: Coincident(g39,g40)
    c: Coincident(g40,g41)
    c: Coincident(g41,g42)
    c: Coincident(g42,g43)
    c: Coincident(g43,g44)
    c: Coincident(g44,g45)
    c: Coincident(g45,g46)
    c: Coincident(g46,g47)
    c: Coincident(g47,g48)
    c: Coincident(g48,g1)
    c: Equal(g1, g2-g48) x47
    c: PointOnObject(g1,g49)
    c: PointOnObject(g2,g49)
    c: PointOnObject(g3,g49)
    c: PointOnObject(g4,g49)
    c: PointOnObject(g5,g49)
    c: PointOnObject(g6,g49)
    c: PointOnObject(g7,g49)
    c: PointOnObject(g8,g49)
    c: PointOnObject(g9,g49)
    c: PointOnObject(g10,g49)
    c: PointOnObject(g11,g49)
    c: PointOnObject(g12,g49)
    c: PointOnObject(g13,g49)
    c: PointOnObject(g14,g49)
    c: PointOnObject(g15,g49)
    c: PointOnObject(g16,g49)
    c: PointOnObject(g17,g49)
    c: PointOnObject(g18,g49)
    c: PointOnObject(g19,g49)
    c: PointOnObject(g20,g49)
    c: PointOnObject(g21,g49)
    c: PointOnObject(g22,g49)
    c: PointOnObject(g23,g49)
    c: PointOnObject(g24,g49)
    c: PointOnObject(g25,g49)
    c: PointOnObject(g26,g49)
    c: PointOnObject(g27,g49)
    c: PointOnObject(g28,g49)
    c: PointOnObject(g29,g49)
    c: PointOnObject(g30,g49)
    c: PointOnObject(g31,g49)
    c: PointOnObject(g32,g49)
    c: PointOnObject(g33,g49)
    c: PointOnObject(g34,g49)
    c: PointOnObject(g35,g49)
    c: PointOnObject(g36,g49)
    c: PointOnObject(g37,g49)
    c: PointOnObject(g38,g49)
    c: PointOnObject(g39,g49)
    c: PointOnObject(g40,g49)
    c: PointOnObject(g41,g49)
    c: PointOnObject(g42,g49)
    c: PointOnObject(g43,g49)
    c: PointOnObject(g44,g49)
    c: PointOnObject(g45,g49)
    c: PointOnObject(g46,g49)
    c: PointOnObject(g47,g49)
    c: PointOnObject(g48,g49)
    c: Coincident(g49,g0)
    c: PointOnObject(g48,g0)
    c: PointOnObject(g1,g-3)
    c: DistanceY(g0,g36) = 0
FEATURE [PartDesign::Pad] Pad215
  BaseFeature = -> Pocket152
  Direction = (0,0,1)
  Length = 1
  Length2 = 10
  Profile = -> Sketch332
  ReferenceAxis = -> Sketch332 [N_Axis]
  Refine = true
  Reversed = true
  Suppressed = false
  Type = 0
FEATURE [PartDesign::Chamfer] Chamfer003
  Angle = 45
  Base = -> Pad215 [Edge137,Edge139,Edge141,Edge143,Edge145,Edge147,Edge149,Edge151,Edge153,Edge135,Edge133,Edge131,Edge129,Edge127,Edge125,Edge123,Edge121,Edge119,Edge117,Edge115,Edge113,Edge111,Edge109,Edge107,Edge105,Edge103,Edge101,Edge194,Edge193,Edge191,Edge189,Edge187,Edge185,Edge183,Edge181,Edge179,Edge177,Edge175,Edge173,Edge171,+8 more]
  BaseFeature = -> Pad215
  ChamferType = 0
  FlipDirection = false
  Refine = true
  Size = 0.99
  Size2 = 1
  SupportTransform = false
  Suppressed = false
  UseAllEdges = false
FEATURE [PartDesign::Pad] Pad216
  BaseFeature = -> Chamfer003
  Direction = (-0.312745,0.634185,0.707107)
  Length = 0.2
  Length2 = 10
  Profile = -> Chamfer003 [Face44]
  Refine = true
  Suppressed = false
  Type = 0
FEATURE [PartDesign::Pad] Pad217
  BaseFeature = -> Pad216
  Direction = (0.587938,-0.392847,0.707107)
  Length = 0.2
  Length2 = 10
  Profile = -> Pad216 [Face45]
  Refine = true
  Suppressed = false
  Type = 0
FEATURE [PartDesign::Pad] Pad218
  BaseFeature = -> Pad217
  Direction = (-0.13795,0.69352,0.707107)
  Length = 0.2
  Length2 = 10
  Profile = -> Pad217 [Face48]
  Refine = true
  Suppressed = false
  Type = 0
FEATURE [PartDesign::Pad] Pad219
  BaseFeature = -> Pad218
  Direction = (0.046247,0.705593,0.707107)
  Length = 0.2
  Length2 = 10
  Profile = -> Pad218 [Face50]
  Refine = true
  Suppressed = false
  Type = 0
FEATURE [PartDesign::Pad] Pad220
  BaseFeature = -> Pad219
  Direction = (0.227292,0.669581,0.707107)
  Length = 0.2
  Length2 = 10
  Profile = -> Pad219 [Face52]
  Refine = true
  Suppressed = false
  Type = 0
FEATURE [PartDesign::Pad] Pad221
  BaseFeature = -> Pad220
  Direction = (0.392847,0.587938,0.707107)
  Length = 0.2
  Length2 = 10
  Profile = -> Pad220 [Face56]
  Refine = true
  Suppressed = false
  Type = 0
FEATURE [PartDesign::Pad] Pad222
  BaseFeature = -> Pad221
  Direction = (0.531631,0.466228,0.707107)
  Length = 0.2
  Length2 = 10
  Profile = -> Pad221 [Face60]
  Refine = true
  Suppressed = false
  Type = 0
FEATURE [PartDesign::Pad] Pad223
  BaseFeature = -> Pad222
  Direction = (0.634185,0.312745,0.707107)
  Length = 0.2
  Length2 = 10
  Profile = -> Pad222 [Face57]
  Refine = true
  Suppressed = false
  Type = 0
FEATURE [PartDesign::Pad] Pad224
  BaseFeature = -> Pad223
  Direction = (-0.466228,0.531631,0.707107)
  Length = 0.2
  Length2 = 10
  Profile = -> Pad223 [Face40]
  Refine = true
  Suppressed = false
  Type = 0
FEATURE [PartDesign::Pad] Pad225
  BaseFeature = -> Pad224
  Direction = (-0.587938,0.392847,0.707107)
  Length = 0.2
  Length2 = 10
  Profile = -> Pad224 [Face36]
  Refine = true
  Suppressed = false
  Type = 0
FEATURE [PartDesign::Pad] Pad226
  BaseFeature = -> Pad225
  Direction = (-0.669581,0.227292,0.707107)
  Length = 0.2
  Length2 = 10
  Profile = -> Pad225 [Face32]
  Refine = true
  Suppressed = false
  Type = 0
FEATURE [PartDesign::Pad] Pad227
  BaseFeature = -> Pad226
  Direction = (-0.705593,0.046247,0.707107)
  Length = 0.2
  Length2 = 10
  Profile = -> Pad226 [Face28]
  Refine = true
  Suppressed = false
  Type = 0
FEATURE [PartDesign::Pad] Pad228
  BaseFeature = -> Pad227
  Direction = (-0.69352,-0.13795,0.707107)
  Length = 0.2
  Length2 = 10
  Profile = -> Pad227 [Face24]
  Refine = true
  Suppressed = false
  Type = 0
FEATURE [PartDesign::Pad] Pad229
  BaseFeature = -> Pad228
  Direction = (-0.634185,-0.312745,0.707107)
  Length = 0.2
  Length2 = 10
  Profile = -> Pad228 [Face20]
  Refine = true
  Suppressed = false
  Type = 0
FEATURE [PartDesign::Pad] Pad230
  BaseFeature = -> Pad229
  Direction = (0.69352,0.13795,0.707107)
  Length = 0.2
  Length2 = 10
  Profile = -> Pad229 [Face53]
  Refine = true
  Suppressed = false
  Type = 0
FEATURE [PartDesign::Pad] Pad231
  BaseFeature = -> Pad230
  Direction = (0.705593,-0.046247,0.707107)
  Length = 0.2
  Length2 = 10
  Profile = -> Pad230 [Face3]
  Refine = true
  Suppressed = false
  Type = 0
FEATURE [PartDesign::Pad] Pad232
  BaseFeature = -> Pad231
  Direction = (0.669581,-0.227292,0.707107)
  Length = 0.2
  Length2 = 10
  Profile = -> Pad231 [Face17]
  Refine = true
  Suppressed = false
  Type = 0
FEATURE [PartDesign::Pad] Pad233
  BaseFeature = -> Pad232
  Direction = (0.466228,-0.531631,0.707107)
  Length = 0.2
  Length2 = 10
  Profile = -> Pad232 [Face99]
  Refine = true
  Suppressed = false
  Type = 0
FEATURE [PartDesign::Pad] Pad234
  BaseFeature = -> Pad233
  Direction = (-0.531631,-0.466228,0.707107)
  Length = 0.2
  Length2 = 10
  Profile = -> Pad233 [Face75]
  Refine = true
  Suppressed = false
  Type = 0
FEATURE [PartDesign::Pad] Pad235
  BaseFeature = -> Pad234
  Direction = (-0.392847,-0.587938,0.707107)
  Length = 0.2
  Length2 = 10
  Profile = -> Pad234 [Face79]
  Refine = true
  Suppressed = false
  Type = 0
FEATURE [PartDesign::Pad] Pad236
  BaseFeature = -> Pad235
  Direction = (-0.227292,-0.669581,0.707107)
  Length = 0.2
  Length2 = 10
  Profile = -> Pad235 [Face83]
  Refine = true
  Suppressed = false
  Type = 0
FEATURE [PartDesign::Pad] Pad237
  BaseFeature = -> Pad236
  Direction = (-0.046247,-0.705593,0.707107)
  Length = 0.2
  Length2 = 10
  Profile = -> Pad236 [Face87]
  Refine = true
  Suppressed = false
  Type = 0
FEATURE [PartDesign::Pad] Pad238
  BaseFeature = -> Pad237
  Direction = (0.312745,-0.634185,0.707107)
  Length = 0.2
  Length2 = 10
  Profile = -> Pad237 [Face95]
  Refine = true
  Suppressed = false
  Type = 0
FEATURE [PartDesign::Pad] Pad239
  BaseFeature = -> Pad238
  Direction = (0.13795,-0.69352,0.707107)
  Length = 0.2
  Length2 = 10
  Profile = -> Pad238 [Face91]
  Refine = true
  Suppressed = false
  Type = 0
FEATURE [Sketcher::SketchObject] Sketch333
  ArcFitTolerance = 1e-06
  AttachmentSupport = -> [Pad239]
  FullyConstrained = true
  MakeInternals = false
  MapMode = 5
  Placement = pos=(0,0,3.6) rot=(0,0,1;0rad)
  sketch-geometry (2):
    g0: Circle CenterX=0 CenterY=0 CenterZ=0 NormalX=0 NormalY=0 NormalZ=1 AngleXU=0 Radius=5.5
    g1: Circle CenterX=0 CenterY=0 CenterZ=0 NormalX=0 NormalY=0 NormalZ=1 AngleXU=0 Radius=4.5
  constraints (4):
    c: Coincident(g0,g-1)
    c: Diameter(g0) = 11
    c: Coincident(g1,g0)
    c: Diameter(g1) = 9
FEATURE [PartDesign::Pocket] Pocket153
  BaseFeature = -> Pad239
  Direction = (0,0,-1)
  Length = 5
  Length2 = 5
  Profile = -> Sketch333 [Edge2,Edge1]
  ReferenceAxis = -> Sketch333 [N_Axis]
  Refine = true
  Reversed = true
  Suppressed = false
  Type = 0
FEATURE [Sketcher::SketchObject] Sketch334
  ArcFitTolerance = 1e-06
  AttachmentSupport = -> [Pocket153]
  ExternalGeometry = -> [Pocket153]
  FullyConstrained = false
  MakeInternals = false
  MapMode = 5
  Placement = pos=(0,0,0) rot=(1,0,0;3.14159rad)
  sketch-geometry (2):
    g0: Circle CenterX=0 CenterY=0 CenterZ=0 NormalX=0 NormalY=0 NormalZ=1 AngleXU=0 Radius=6.05
    g1: Circle CenterX=0 CenterY=0 CenterZ=0 NormalX=0 NormalY=0 NormalZ=1 AngleXU=0 Radius=6.5
  constraints (3):
    c: Coincident(g0,g-1)
    c: Coincident(g1,g0)
    c: Diameter(g1) = 13
FEATURE [PartDesign::Pocket] Pocket154
  BaseFeature = -> Pocket153
  Direction = (0,0,1)
  Length = 5
  Length2 = 5
  Profile = -> Sketch334
  ReferenceAxis = -> Sketch334 [N_Axis]
  Refine = true
  Suppressed = false
  Type = 0
FEATURE [Sketcher::SketchObject] Sketch335
  ArcFitTolerance = 1e-06
  AttachmentSupport = -> [Pocket154]
  FullyConstrained = true
  MakeInternals = false
  MapMode = 5
  Placement = pos=(0,0,4.1) rot=(0,0,1;0rad)
  sketch-geometry (1):
    g0: Circle CenterX=0 CenterY=0 CenterZ=0 NormalX=0 NormalY=0 NormalZ=1 AngleXU=0 Radius=1.05
  constraints (2):
    c: Coincident(g0,g-1)
    c: Diameter(g0) = 2.1
FEATURE [PartDesign::Pocket] Pocket155
  BaseFeature = -> Pocket154
  Direction = (0,0,-1)
  Length = 5
  Length2 = 5
  Profile = -> Sketch335
  ReferenceAxis = -> Sketch335 [N_Axis]
  Refine = true
  Suppressed = false
  Type = 0
FEATURE [Sketcher::SketchObject] Sketch336
  ArcFitTolerance = 1e-06
  AttachmentSupport = -> [Pocket155]
  FullyConstrained = true
  MakeInternals = false
  MapMode = 5
  Placement = pos=(0,0,4.1) rot=(0,0,1;0rad)
  sketch-geometry (1):
    g0: Circle CenterX=0 CenterY=0 CenterZ=0 NormalX=0 NormalY=0 NormalZ=1 AngleXU=0 Radius=1.75
  constraints (2):
    c: Coincident(g0,g-1)
    c: Diameter(g0) = 3.5
FEATURE [PartDesign::Pocket] Pocket156
  BaseFeature = -> Pocket155
  Direction = (0,0,-1)
  Length = 1
  Length2 = 5
  Profile = -> Sketch336
  ReferenceAxis = -> Sketch336 [N_Axis]
  Refine = true
  Suppressed = false
  Type = 0
FEATURE [Sketcher::SketchObject] Sketch337
  ArcFitTolerance = 1e-06
  AttachmentSupport = -> [Pocket156]
  ExternalGeometry = -> [Pocket156]
  FullyConstrained = true
  MakeInternals = false
  MapMode = 5
  Placement = pos=(0,0,4.1) rot=(0,0,1;0rad)
  sketch-geometry (12):
    g0: Circle CenterX=0 CenterY=2.65 CenterZ=0 NormalX=0 NormalY=0 NormalZ=1 AngleXU=0 Radius=0.25
    g1: Circle CenterX=2.65 CenterY=0 CenterZ=0 NormalX=0 NormalY=0 NormalZ=1 AngleXU=0 Radius=0.25
    g2: Circle CenterX=0 CenterY=-2.65 CenterZ=0 NormalX=0 NormalY=0 NormalZ=1 AngleXU=0 Radius=0.25
    g3: Circle CenterX=-2.65 CenterY=0 CenterZ=0 NormalX=0 NormalY=0 NormalZ=1 AngleXU=0 Radius=0.25
    g4: Circle CenterX=1.87383 CenterY=1.87383 CenterZ=0 NormalX=0 NormalY=0 NormalZ=1 AngleXU=0 Radius=0.25
    g5: Circle CenterX=1.87383 CenterY=-1.87383 CenterZ=0 NormalX=0 NormalY=0 NormalZ=1 AngleXU=0 Radius=0.25
    g6: Circle CenterX=-1.87383 CenterY=-1.87383 CenterZ=0 NormalX=0 NormalY=0 NormalZ=1 AngleXU=0 Radius=0.25
    g7: Circle CenterX=-1.87383 CenterY=1.87383 CenterZ=0 NormalX=0 NormalY=0 NormalZ=1 AngleXU=0 Radius=0.25
    g8: LineSegment StartX=1.87383 StartY=1.87383 StartZ=0 EndX=0 EndY=0 EndZ=0
    g9: LineSegment StartX=0 StartY=0 StartZ=0 EndX=1.87383 EndY=-1.87383 EndZ=0
    g10: LineSegment StartX=0 StartY=0 StartZ=0 EndX=-1.87383 EndY=-1.87383 EndZ=0
    g11: LineSegment StartX=0 StartY=0 StartZ=0 EndX=-1.87383 EndY=1.87383 EndZ=0
  constraints (34):
    c: PointOnObject(g0,g-2)
    c: Diameter(g-3) = 7.1
    c: Diameter(g-4) = 3.5
    c: DistanceY(g-1,g0) = 2.65
    c: Diameter(g0) = 0.5
    c: PointOnObject(g1,g-1)
    c: PointOnObject(g2,g-2)
    c: PointOnObject(g3,g-1)
    c: Diameter(g3) = 0.5
    c: Diameter(g1) = 0.5
    c: Diameter(g2) = 0.5
    c: DistanceX(g3,g-1) = 2.65
    c: DistanceX(g-1,g1) = 2.65
    c: DistanceY(g2,g-1) = 2.65
    c: Diameter(g7) = 0.5
    c: Diameter(g4) = 0.5
    c: Diameter(g5) = 0.5
    c: Diameter(g6) = 0.5
    c: Distance(g-1,g6) = 2.65
    c: Distance(g-1,g5) = 2.65
    c: Distance(g-1,g4) = 2.65
    c: Distance(g-1,g7) = 2.65
    c: Coincident(g8,g4)
    c: Coincident(g8,g-1)
    c: Angle(g-1,g8) = 0.785398
    c: Coincident(g9,g8)
    c: Coincident(g9,g5)
    c: Coincident(g10,g8)
    c: Coincident(g10,g6)
    c: Coincident(g11,g8)
    c: Coincident(g11,g7)
    c: Angle(g9,g-1) = 0.785398
    c: Angle(g-2,g10) = 2.35619
    c: Angle(g-1,g11) = 2.35619
FEATURE [PartDesign::Pocket] Pocket157
  BaseFeature = -> Pocket156
  Direction = (0,0,-1)
  Length = 0.2
  Length2 = 5
  Profile = -> Sketch337 [Edge8,Edge4,Edge7,Edge3,Edge6,Edge2,Edge5,Edge1]
  ReferenceAxis = -> Sketch337 [N_Axis]
  Refine = true
  Suppressed = false
  Type = 0
FEATURE [Sketcher::SketchObject] Sketch338
  ArcFitTolerance = 1e-06
  AttachmentSupport = -> [Pocket157]
  FullyConstrained = true
  MakeInternals = false
  MapMode = 5
  Placement = pos=(0,0,0) rot=(1,0,0;3.14159rad)
  sketch-geometry (1):
    g0: Circle CenterX=0 CenterY=0 CenterZ=0 NormalX=0 NormalY=0 NormalZ=1 AngleXU=0 Radius=2.5
  constraints (2):
    c: Coincident(g0,g-1)
    c: Diameter(g0) = 5
FEATURE [PartDesign::Pocket] Pocket158
  BaseFeature = -> Pocket157
  Direction = (0,0,1)
  Length = 1.5
  Length2 = 5
  Profile = -> Sketch338
  ReferenceAxis = -> Sketch338 [N_Axis]
  Refine = true
  Suppressed = false
  Type = 0
FEATURE [Sketcher::SketchObject] Sketch339
  ArcFitTolerance = 1e-06
  AttachmentSupport = -> [Pocket158]
  FullyConstrained = true
  MakeInternals = false
  MapMode = 5
  Placement = pos=(0,0,0) rot=(1,0,0;3.14159rad)
  sketch-geometry (2):
    g0: Circle CenterX=0 CenterY=0 CenterZ=0 NormalX=0 NormalY=0 NormalZ=1 AngleXU=0 Radius=4.75
    g1: Circle CenterX=0 CenterY=0 CenterZ=0 NormalX=0 NormalY=0 NormalZ=1 AngleXU=0 Radius=5.5
  constraints (4):
    c: Coincident(g0,g-1)
    c: Coincident(g1,g0)
    c: Diameter(g0) = 9.5
    c: Diameter(g1) = 11
FEATURE [PartDesign::Pocket] Pocket159
  BaseFeature = -> Pocket158
  Direction = (0,0,1)
  Length = 1.5
  Length2 = 5
  Profile = -> Sketch339
  ReferenceAxis = -> Sketch339 [N_Axis]
  Refine = true
  Suppressed = false
  Type = 0
FEATURE [PartDesign::Body] Body023  label="Tire1"
  AllowCompound = false
  Group = -> [Sketch329,Pad213,Sketch330,Pad214,Sketch331,Pocket152,Sketch332,Pad215,Chamfer003,Pad216,Pad217,Pad218,Pad219,Pad220,Pad221,Pad222,Pad223,Pad224,Pad225,Pad226,Pad227,Pad228,Pad229,Pad230,Pad231,Pad232,Pad233,Pad234,Pad235,Pad236,Pad237,Pad238,Pad239,Sketch333,Pocket153,Sketch334,Pocket154,Sketch335,Pocket155,Sketch336,Pocket156,Sketch337,Pocket157,Sketch338,Pocket158,Sketch339,Pocket159]
  Origin = -> Origin024
  Placement = pos=(31.8,-26.27,-7) rot=(-0.707107,0,-0.707107;3.14159rad)
  Tip = -> Pocket159
COMPONENT P22 — same part as P21; its construction recipe is shown at P21.
COMPONENT P23 — same part as P21; its construction recipe is shown at P21.
COMPONENT P24 — same part as P21; its construction recipe is shown at P21.
COMPONENT P25 — same part as P21; its construction recipe is shown at P21.
